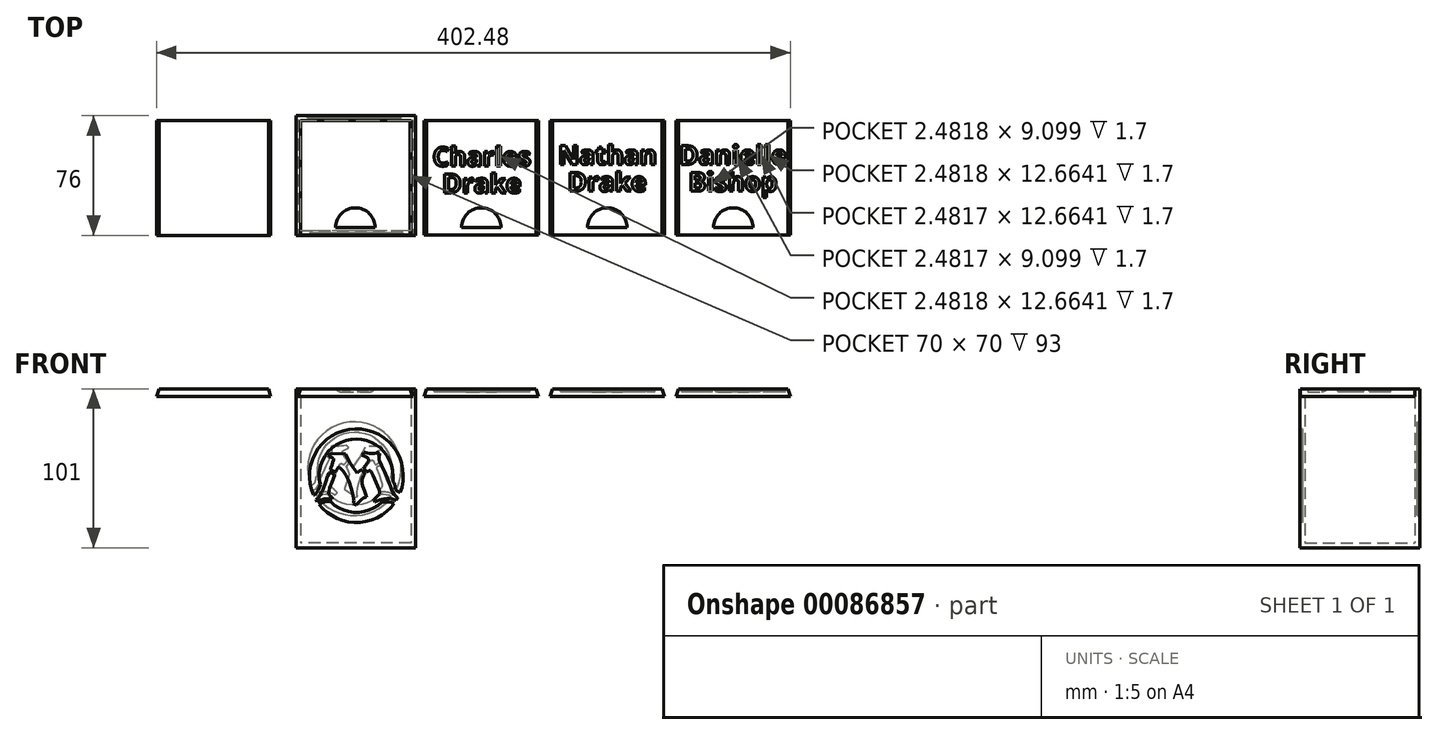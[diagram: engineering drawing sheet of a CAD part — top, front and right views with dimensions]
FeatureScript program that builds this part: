
annotation { "Feature Type Name" : "Feature", "Feature Type Description" : "" }
export const myFeature = defineFeature(function(context is Context, id is Id, definition is map)
    precondition{}
    {
        {
            var Q0;
            Q0=qCreatedBy(makeId("Top.planeOp"),FACE);
            var sketch = newSketch(context, id + "F0", { "sketchPlane" : qUnion([Q0])});
            skLineSegment(sketch, "E0.bottom", {"start": v(35, -35) * mm, "end": v(-35, -35) * mm});
            skLineSegment(sketch, "E0.top", {"start": v(35, 35) * mm, "end": v(-35, 35) * mm});
            skLineSegment(sketch, "E0.left", {"start": v(35, -35) * mm, "end": v(35, 35) * mm});
            skLineSegment(sketch, "E0.right", {"start": v(-35, -35) * mm, "end": v(-35, 35) * mm});
            skPoint(sketch, "E0.middle", {"position": v(0, 0) * mm});
            skLineSegment(sketch, "E1.0", {"start": v(38, 38) * mm, "end": v(-38, 38) * mm});
            skLineSegment(sketch, "E1.1", {"start": v(38, -38) * mm, "end": v(38, 38) * mm});
            skLineSegment(sketch, "E1.2", {"start": v(38, -38) * mm, "end": v(-38, -38) * mm});
            skLineSegment(sketch, "E1.3", {"start": v(-38, -38) * mm, "end": v(-38, 38) * mm});
            skSolve(sketch);
        }
        {
            var Q0;
            Q0=makeQuery(id+"F0.imprint","IMPRINT",FACE,{"disambiguationData":[TD([[makeQuery(id+"F0.imprint","IMPRINT",EDGE,{"derivedFrom":sQuery(id+"F0.wireOp",EDGE,"E0.bottom")}),-1.0]])]});
            var Q1;
            Q1=makeQuery(id+"F0.imprint","IMPRINT",FACE,{"disambiguationData":[TD([[makeQuery(id+"F0.imprint","IMPRINT",EDGE,{"derivedFrom":sQuery(id+"F0.wireOp",EDGE,"E0.bottom")}),1.0]])]});
            extrude(context, id + "F1", {"entities" : qUnion([Q0, Q1]), "depth" : 101 * mm});
        }
        {
            var Q0;
            Q0=makeQuery(id+"F1.opExtrude","CAP_FACE",FACE,{"disambiguationData":[OSD([sQuery(id+"F0.wireOp",EDGE,"E1.0"),sQuery(id+"F0.wireOp",EDGE,"E1.1"),sQuery(id+"F0.wireOp",EDGE,"E1.2"),sQuery(id+"F0.wireOp",EDGE,"E1.3")])],"isStart":false});
            shell(context, id + "F2", {"entities" : qUnion([Q0]), "thickness" : 3 * mm});
        }
        {
            var Q0;
            Q0=makeQuery(id+"F1.opExtrude","SWEPT_FACE",FACE,{"disambiguationData":[OSD([sQuery(id+"F0.wireOp",EDGE,"E1.2")])]});
            var sketch = newSketch(context, id + "F3", { "sketchPlane" : qUnion([Q0])});
            skLineSegment(sketch, "E2", {"start": v(-4.3, 75.14) * mm, "end": v(-0.4, 75.51) * mm});
            skLineSegment(sketch, "E3", {"start": v(-8.13, 74.27) * mm, "end": v(-4.3, 75.14) * mm});
            skLineSegment(sketch, "E4", {"start": v(-11.8, 72.9) * mm, "end": v(-8.13, 74.27) * mm});
            skLineSegment(sketch, "E5", {"start": v(-15.26, 71.06) * mm, "end": v(-11.8, 72.9) * mm});
            skLineSegment(sketch, "E6", {"start": v(-18.45, 68.78) * mm, "end": v(-15.26, 71.06) * mm});
            skLineSegment(sketch, "E7", {"start": v(-21.3, 66.1) * mm, "end": v(-18.45, 68.78) * mm});
            skLineSegment(sketch, "E8", {"start": v(-23.8, 63.06) * mm, "end": v(-21.3, 66.1) * mm});
            skLineSegment(sketch, "E9", {"start": v(-25.85, 59.73) * mm, "end": v(-23.8, 63.06) * mm});
            skLineSegment(sketch, "E10", {"start": v(-27.46, 56.16) * mm, "end": v(-25.85, 59.73) * mm});
            skLineSegment(sketch, "E11", {"start": v(-28.58, 52.4) * mm, "end": v(-27.46, 56.16) * mm});
            skLineSegment(sketch, "E12", {"start": v(-29.2, 48.53) * mm, "end": v(-28.58, 52.4) * mm});
            skLineSegment(sketch, "E13", {"start": v(-29.31, 44.61) * mm, "end": v(-29.2, 48.53) * mm});
            skLineSegment(sketch, "E14", {"start": v(-28.9, 40.72) * mm, "end": v(-29.31, 44.61) * mm});
            skLineSegment(sketch, "E15", {"start": v(-27.98, 36.9) * mm, "end": v(-28.9, 40.72) * mm});
            skLineSegment(sketch, "E16", {"start": v(-26.65, 33.46) * mm, "end": v(-27.98, 36.9) * mm});
            skLineSegment(sketch, "E17", {"start": v(-26.36, 33.55) * mm, "end": v(-26.65, 33.46) * mm});
            skLineSegment(sketch, "E18", {"start": v(-26.15, 33.66) * mm, "end": v(-26.36, 33.55) * mm});
            skLineSegment(sketch, "E19", {"start": v(-25.97, 33.78) * mm, "end": v(-26.15, 33.66) * mm});
            skLineSegment(sketch, "E20", {"start": v(-25.26, 34.57) * mm, "end": v(-25.97, 33.78) * mm});
            skLineSegment(sketch, "E21", {"start": v(-24.07, 36.37) * mm, "end": v(-25.26, 34.57) * mm});
            skLineSegment(sketch, "E22", {"start": v(-22.46, 40.36) * mm, "end": v(-24.07, 36.37) * mm});
            skLineSegment(sketch, "E23", {"start": v(-23, 42.05) * mm, "end": v(-22.46, 40.36) * mm});
            skLineSegment(sketch, "E24", {"start": v(-23.3, 43.9) * mm, "end": v(-23, 42.05) * mm});
            skLineSegment(sketch, "E25", {"start": v(-23.33, 45.77) * mm, "end": v(-23.3, 43.9) * mm});
            skLineSegment(sketch, "E26", {"start": v(-23.33, 46.03) * mm, "end": v(-23.33, 45.77) * mm});
            skLineSegment(sketch, "E27", {"start": v(-23.33, 46.29) * mm, "end": v(-23.33, 46.03) * mm});
            skLineSegment(sketch, "E28", {"start": v(-23.3, 46.8) * mm, "end": v(-23.33, 46.29) * mm});
            skLineSegment(sketch, "E29", {"start": v(-23.24, 47.82) * mm, "end": v(-23.3, 46.8) * mm});
            skLineSegment(sketch, "E30", {"start": v(-23.08, 49.13) * mm, "end": v(-23.24, 47.82) * mm});
            skLineSegment(sketch, "E31", {"start": v(-22.36, 52.4) * mm, "end": v(-23.08, 49.13) * mm});
            skLineSegment(sketch, "E32", {"start": v(-21.16, 55.55) * mm, "end": v(-22.36, 52.4) * mm});
            skLineSegment(sketch, "E33", {"start": v(-19.53, 58.49) * mm, "end": v(-21.16, 55.55) * mm});
            skLineSegment(sketch, "E34", {"start": v(-17.49, 61.16) * mm, "end": v(-19.53, 58.49) * mm});
            skLineSegment(sketch, "E35", {"start": v(-15.09, 63.51) * mm, "end": v(-17.49, 61.16) * mm});
            skLineSegment(sketch, "E36", {"start": v(-12.37, 65.5) * mm, "end": v(-15.09, 63.51) * mm});
            skLineSegment(sketch, "E37", {"start": v(-9.4, 67.06) * mm, "end": v(-12.37, 65.5) * mm});
            skLineSegment(sketch, "E38", {"start": v(-6.23, 68.19) * mm, "end": v(-9.4, 67.06) * mm});
            skLineSegment(sketch, "E39", {"start": v(-2.94, 68.84) * mm, "end": v(-6.23, 68.19) * mm});
            skLineSegment(sketch, "E40", {"start": v(-2.85, 68.86) * mm, "end": v(-2.94, 68.84) * mm});
            skLineSegment(sketch, "E41", {"start": v(-2.77, 68.87) * mm, "end": v(-2.85, 68.86) * mm});
            skLineSegment(sketch, "E42", {"start": v(-2.6, 68.88) * mm, "end": v(-2.77, 68.87) * mm});
            skLineSegment(sketch, "E43", {"start": v(-2.26, 68.92) * mm, "end": v(-2.6, 68.88) * mm});
            skLineSegment(sketch, "E44", {"start": v(0.42, 69.02) * mm, "end": v(-2.26, 68.92) * mm});
            skLineSegment(sketch, "E45", {"start": v(3.73, 68.79) * mm, "end": v(0.42, 69.02) * mm});
            skLineSegment(sketch, "E46", {"start": v(6.97, 68.08) * mm, "end": v(3.73, 68.79) * mm});
            skLineSegment(sketch, "E47", {"start": v(10.08, 66.92) * mm, "end": v(6.97, 68.08) * mm});
            skLineSegment(sketch, "E48", {"start": v(12.99, 65.33) * mm, "end": v(10.08, 66.92) * mm});
            skLineSegment(sketch, "E49", {"start": v(15.64, 63.34) * mm, "end": v(12.99, 65.33) * mm});
            skLineSegment(sketch, "E50", {"start": v(17.99, 61) * mm, "end": v(15.64, 63.34) * mm});
            skLineSegment(sketch, "E51", {"start": v(19.98, 58.34) * mm, "end": v(17.99, 61) * mm});
            skLineSegment(sketch, "E52", {"start": v(21.57, 55.43) * mm, "end": v(19.98, 58.34) * mm});
            skLineSegment(sketch, "E53", {"start": v(22.73, 52.32) * mm, "end": v(21.57, 55.43) * mm});
            skLineSegment(sketch, "E54", {"start": v(23.43, 49.09) * mm, "end": v(22.73, 52.32) * mm});
            skLineSegment(sketch, "E55", {"start": v(23.44, 49) * mm, "end": v(23.43, 49.09) * mm});
            skLineSegment(sketch, "E56", {"start": v(23.45, 48.92) * mm, "end": v(23.44, 49) * mm});
            skLineSegment(sketch, "E57", {"start": v(23.47, 48.75) * mm, "end": v(23.45, 48.92) * mm});
            skLineSegment(sketch, "E58", {"start": v(23.52, 48.42) * mm, "end": v(23.47, 48.75) * mm});
            skLineSegment(sketch, "E59", {"start": v(23.67, 45.78) * mm, "end": v(23.52, 48.42) * mm});
            skLineSegment(sketch, "E60", {"start": v(23.65, 42.52) * mm, "end": v(23.67, 45.78) * mm});
            skLineSegment(sketch, "E61", {"start": v(23.69, 42.15) * mm, "end": v(23.65, 42.52) * mm});
            skLineSegment(sketch, "E62", {"start": v(23.79, 41.8) * mm, "end": v(23.69, 42.15) * mm});
            skLineSegment(sketch, "E63", {"start": v(24.17, 41.13) * mm, "end": v(23.79, 41.8) * mm});
            skLineSegment(sketch, "E64", {"start": v(24.62, 40.42) * mm, "end": v(24.17, 41.13) * mm});
            skLineSegment(sketch, "E65", {"start": v(24.77, 40) * mm, "end": v(24.62, 40.42) * mm});
            skLineSegment(sketch, "E66", {"start": v(24.85, 39.58) * mm, "end": v(24.77, 40) * mm});
            skLineSegment(sketch, "E67", {"start": v(25.07, 37.97) * mm, "end": v(24.85, 39.58) * mm});
            skLineSegment(sketch, "E68", {"start": v(25.33, 37.24) * mm, "end": v(25.07, 37.97) * mm});
            skLineSegment(sketch, "E69", {"start": v(25.51, 36.92) * mm, "end": v(25.33, 37.24) * mm});
            skLineSegment(sketch, "E70", {"start": v(25.74, 36.63) * mm, "end": v(25.51, 36.92) * mm});
            skLineSegment(sketch, "E71", {"start": v(26.32, 36.12) * mm, "end": v(25.74, 36.63) * mm});
            skLineSegment(sketch, "E72", {"start": v(27, 35.67) * mm, "end": v(26.32, 36.12) * mm});
            skLineSegment(sketch, "E73", {"start": v(28.14, 35.03) * mm, "end": v(27, 35.67) * mm});
            skLineSegment(sketch, "E74", {"start": v(29.26, 38.49) * mm, "end": v(28.14, 35.03) * mm});
            skLineSegment(sketch, "E75", {"start": v(29.97, 42.34) * mm, "end": v(29.26, 38.49) * mm});
            skLineSegment(sketch, "E76", {"start": v(30.16, 46.26) * mm, "end": v(29.97, 42.34) * mm});
            skLineSegment(sketch, "E77", {"start": v(29.84, 50.16) * mm, "end": v(30.16, 46.26) * mm});
            skLineSegment(sketch, "E78", {"start": v(29, 54) * mm, "end": v(29.84, 50.16) * mm});
            skLineSegment(sketch, "E79", {"start": v(27.68, 57.68) * mm, "end": v(29, 54) * mm});
            skLineSegment(sketch, "E80", {"start": v(25.88, 61.16) * mm, "end": v(27.68, 57.68) * mm});
            skLineSegment(sketch, "E81", {"start": v(23.63, 64.37) * mm, "end": v(25.88, 61.16) * mm});
            skLineSegment(sketch, "E82", {"start": v(20.99, 67.26) * mm, "end": v(23.63, 64.37) * mm});
            skLineSegment(sketch, "E83", {"start": v(17.98, 69.78) * mm, "end": v(20.99, 67.26) * mm});
            skLineSegment(sketch, "E84", {"start": v(14.67, 71.88) * mm, "end": v(17.98, 69.78) * mm});
            skLineSegment(sketch, "E85", {"start": v(11.12, 73.53) * mm, "end": v(14.67, 71.88) * mm});
            skLineSegment(sketch, "E86", {"start": v(7.38, 74.7) * mm, "end": v(11.12, 73.53) * mm});
            skLineSegment(sketch, "E87", {"start": v(3.51, 75.36) * mm, "end": v(7.38, 74.7) * mm});
            skLineSegment(sketch, "E88", {"start": v(-0.4, 75.51) * mm, "end": v(3.51, 75.36) * mm});
            skLineSegment(sketch, "E89", {"start": v(6.66, 32.96) * mm, "end": v(6.68, 32.9) * mm});
            skLineSegment(sketch, "E90", {"start": v(6.65, 33.01) * mm, "end": v(6.66, 32.96) * mm});
            skLineSegment(sketch, "E91", {"start": v(6.61, 33.12) * mm, "end": v(6.65, 33.01) * mm});
            skLineSegment(sketch, "E92", {"start": v(6.55, 33.33) * mm, "end": v(6.61, 33.12) * mm});
            skLineSegment(sketch, "E93", {"start": v(5.67, 36.09) * mm, "end": v(6.55, 33.33) * mm});
            skLineSegment(sketch, "E94", {"start": v(4.49, 39.23) * mm, "end": v(5.67, 36.09) * mm});
            skLineSegment(sketch, "E95", {"start": v(4.05, 40.87) * mm, "end": v(4.49, 39.23) * mm});
            skLineSegment(sketch, "E96", {"start": v(3.93, 41.74) * mm, "end": v(4.05, 40.87) * mm});
            skLineSegment(sketch, "E97", {"start": v(3.93, 42.61) * mm, "end": v(3.93, 41.74) * mm});
            skLineSegment(sketch, "E98", {"start": v(4.06, 43.48) * mm, "end": v(3.93, 42.61) * mm});
            skLineSegment(sketch, "E99", {"start": v(4.3, 44.31) * mm, "end": v(4.06, 43.48) * mm});
            skLineSegment(sketch, "E100", {"start": v(4.98, 45.9) * mm, "end": v(4.3, 44.31) * mm});
            skLineSegment(sketch, "E101", {"start": v(5.57, 46.73) * mm, "end": v(4.98, 45.9) * mm});
            skLineSegment(sketch, "E102", {"start": v(5.59, 46.79) * mm, "end": v(5.57, 46.73) * mm});
            skLineSegment(sketch, "E103", {"start": v(5.6, 46.86) * mm, "end": v(5.59, 46.79) * mm});
            skLineSegment(sketch, "E104", {"start": v(5.57, 47.1) * mm, "end": v(5.6, 46.86) * mm});
            skLineSegment(sketch, "E105", {"start": v(5.54, 47.33) * mm, "end": v(5.57, 47.1) * mm});
            skLineSegment(sketch, "E106", {"start": v(5.51, 47.42) * mm, "end": v(5.54, 47.33) * mm});
            skLineSegment(sketch, "E107", {"start": v(5.5, 47.46) * mm, "end": v(5.51, 47.42) * mm});
            skLineSegment(sketch, "E108", {"start": v(4.16, 49) * mm, "end": v(5.5, 47.46) * mm});
            skLineSegment(sketch, "E109", {"start": v(4, 49.15) * mm, "end": v(4.16, 49) * mm});
            skLineSegment(sketch, "E110", {"start": v(3.82, 49.26) * mm, "end": v(4, 49.15) * mm});
            skLineSegment(sketch, "E111", {"start": v(3.64, 49.33) * mm, "end": v(3.82, 49.26) * mm});
            skLineSegment(sketch, "E112", {"start": v(3.44, 49.35) * mm, "end": v(3.64, 49.33) * mm});
            skLineSegment(sketch, "E113", {"start": v(2.98, 49.29) * mm, "end": v(3.44, 49.35) * mm});
            skLineSegment(sketch, "E114", {"start": v(2.78, 49.23) * mm, "end": v(2.98, 49.29) * mm});
            skLineSegment(sketch, "E115", {"start": v(2.6, 49.13) * mm, "end": v(2.78, 49.23) * mm});
            skLineSegment(sketch, "E116", {"start": v(0.88, 47.6) * mm, "end": v(2.6, 49.13) * mm});
            skLineSegment(sketch, "E117", {"start": v(0.21, 48.5) * mm, "end": v(0.88, 47.6) * mm});
            skLineSegment(sketch, "E118", {"start": v(-1.7, 51.18) * mm, "end": v(0.21, 48.5) * mm});
            skLineSegment(sketch, "E119", {"start": v(-3.45, 53.97) * mm, "end": v(-1.7, 51.18) * mm});
            skLineSegment(sketch, "E120", {"start": v(-3.45, 53.97) * mm, "end": v(-5.11, 56.82) * mm});
            skLineSegment(sketch, "E121", {"start": v(-5.11, 56.82) * mm, "end": v(-6.54, 59.63) * mm});
            skLineSegment(sketch, "E122", {"start": v(-16.46, 59.92) * mm, "end": v(-6.54, 59.63) * mm});
            skLineSegment(sketch, "E123", {"start": v(-17.38, 58.63) * mm, "end": v(-16.46, 59.92) * mm});
            skLineSegment(sketch, "E124", {"start": v(-17.61, 58.29) * mm, "end": v(-17.38, 58.63) * mm});
            skLineSegment(sketch, "E125", {"start": v(-17.55, 58.21) * mm, "end": v(-17.61, 58.29) * mm});
            skLineSegment(sketch, "E126", {"start": v(-17.24, 57.94) * mm, "end": v(-17.55, 58.21) * mm});
            skLineSegment(sketch, "E127", {"start": v(-17.1, 57.86) * mm, "end": v(-17.24, 57.94) * mm});
            skLineSegment(sketch, "E128", {"start": v(-16.95, 57.8) * mm, "end": v(-17.1, 57.86) * mm});
            skLineSegment(sketch, "E129", {"start": v(-16.1, 57.7) * mm, "end": v(-16.95, 57.8) * mm});
            skLineSegment(sketch, "E130", {"start": v(-15.27, 57.4) * mm, "end": v(-16.1, 57.7) * mm});
            skLineSegment(sketch, "E131", {"start": v(-14.83, 57.2) * mm, "end": v(-15.27, 57.4) * mm});
            skLineSegment(sketch, "E132", {"start": v(-14.6, 57.08) * mm, "end": v(-14.83, 57.2) * mm});
            skLineSegment(sketch, "E133", {"start": v(-14.4, 56.92) * mm, "end": v(-14.6, 57.08) * mm});
            skLineSegment(sketch, "E134", {"start": v(-14.3, 56.8) * mm, "end": v(-14.4, 56.92) * mm});
            skLineSegment(sketch, "E135", {"start": v(-14.22, 56.66) * mm, "end": v(-14.3, 56.8) * mm});
            skLineSegment(sketch, "E136", {"start": v(-14.18, 56.52) * mm, "end": v(-14.22, 56.66) * mm});
            skLineSegment(sketch, "E137", {"start": v(-14.17, 56.37) * mm, "end": v(-14.18, 56.52) * mm});
            skLineSegment(sketch, "E138", {"start": v(-14.2, 55.88) * mm, "end": v(-14.17, 56.37) * mm});
            skLineSegment(sketch, "E139", {"start": v(-14.58, 54.18) * mm, "end": v(-14.2, 55.88) * mm});
            skLineSegment(sketch, "E140", {"start": v(-15.2, 52.54) * mm, "end": v(-14.58, 54.18) * mm});
            skLineSegment(sketch, "E141", {"start": v(-15.82, 50.95) * mm, "end": v(-15.2, 52.54) * mm});
            skLineSegment(sketch, "E142", {"start": v(-15.96, 50.54) * mm, "end": v(-15.82, 50.95) * mm});
            skLineSegment(sketch, "E143", {"start": v(-16.04, 50.16) * mm, "end": v(-15.96, 50.54) * mm});
            skLineSegment(sketch, "E144", {"start": v(-16.03, 50.02) * mm, "end": v(-16.04, 50.16) * mm});
            skLineSegment(sketch, "E145", {"start": v(-15.99, 49.87) * mm, "end": v(-16.03, 50.02) * mm});
            skLineSegment(sketch, "E146", {"start": v(-15.9, 49.73) * mm, "end": v(-15.99, 49.87) * mm});
            skLineSegment(sketch, "E147", {"start": v(-15.8, 49.6) * mm, "end": v(-15.9, 49.73) * mm});
            skLineSegment(sketch, "E148", {"start": v(-15.65, 49.5) * mm, "end": v(-15.8, 49.6) * mm});
            skLineSegment(sketch, "E149", {"start": v(-15.49, 49.42) * mm, "end": v(-15.65, 49.5) * mm});
            skLineSegment(sketch, "E150", {"start": v(-15.09, 49.27) * mm, "end": v(-15.49, 49.42) * mm});
            skLineSegment(sketch, "E151", {"start": v(-14.3, 48.91) * mm, "end": v(-15.09, 49.27) * mm});
            skLineSegment(sketch, "E152", {"start": v(-13.51, 48.5) * mm, "end": v(-14.3, 48.91) * mm});
            skLineSegment(sketch, "E153", {"start": v(-13.34, 48.44) * mm, "end": v(-13.51, 48.5) * mm});
            skLineSegment(sketch, "E154", {"start": v(-13.18, 48.4) * mm, "end": v(-13.34, 48.44) * mm});
            skLineSegment(sketch, "E155", {"start": v(-13.11, 48.4) * mm, "end": v(-13.18, 48.4) * mm});
            skLineSegment(sketch, "E156", {"start": v(-13.05, 48.41) * mm, "end": v(-13.11, 48.4) * mm});
            skLineSegment(sketch, "E157", {"start": v(-12.9, 48.46) * mm, "end": v(-13.05, 48.41) * mm});
            skLineSegment(sketch, "E158", {"start": v(-12.75, 48.55) * mm, "end": v(-12.9, 48.46) * mm});
            skLineSegment(sketch, "E159", {"start": v(-12.62, 48.66) * mm, "end": v(-12.75, 48.55) * mm});
            skLineSegment(sketch, "E160", {"start": v(-12.38, 48.98) * mm, "end": v(-12.62, 48.66) * mm});
            skLineSegment(sketch, "E161", {"start": v(-12, 49.71) * mm, "end": v(-12.38, 48.98) * mm});
            skLineSegment(sketch, "E162", {"start": v(-11.65, 50.54) * mm, "end": v(-12, 49.71) * mm});
            skLineSegment(sketch, "E163", {"start": v(-11.54, 50.76) * mm, "end": v(-11.65, 50.54) * mm});
            skLineSegment(sketch, "E164", {"start": v(-11.47, 50.88) * mm, "end": v(-11.54, 50.76) * mm});
            skLineSegment(sketch, "E165", {"start": v(-11.36, 51) * mm, "end": v(-11.47, 50.88) * mm});
            skLineSegment(sketch, "E166", {"start": v(-11.24, 51.08) * mm, "end": v(-11.36, 51) * mm});
            skLineSegment(sketch, "E167", {"start": v(-11.08, 51.13) * mm, "end": v(-11.24, 51.08) * mm});
            skLineSegment(sketch, "E168", {"start": v(-10.93, 51.15) * mm, "end": v(-11.08, 51.13) * mm});
            skLineSegment(sketch, "E169", {"start": v(-10.78, 51.14) * mm, "end": v(-10.93, 51.15) * mm});
            skLineSegment(sketch, "E170", {"start": v(-10.52, 51.09) * mm, "end": v(-10.78, 51.14) * mm});
            skLineSegment(sketch, "E171", {"start": v(-10.28, 51) * mm, "end": v(-10.52, 51.09) * mm});
            skLineSegment(sketch, "E172", {"start": v(-9.88, 50.75) * mm, "end": v(-10.28, 51) * mm});
            skLineSegment(sketch, "E173", {"start": v(-9.88, 50.75) * mm, "end": v(-9.18, 50.19) * mm});
            skLineSegment(sketch, "E174", {"start": v(-9.18, 50.19) * mm, "end": v(-8, 48.88) * mm});
            skLineSegment(sketch, "E175", {"start": v(-6.22, 45.9) * mm, "end": v(-8, 48.88) * mm});
            skLineSegment(sketch, "E176", {"start": v(-4.98, 43.52) * mm, "end": v(-6.22, 45.9) * mm});
            skLineSegment(sketch, "E177", {"start": v(-3.87, 41.07) * mm, "end": v(-4.98, 43.52) * mm});
            skLineSegment(sketch, "E178", {"start": v(-2.37, 35.93) * mm, "end": v(-3.87, 41.07) * mm});
            skLineSegment(sketch, "E179", {"start": v(-1.74, 33.34) * mm, "end": v(-2.37, 35.93) * mm});
            skLineSegment(sketch, "E180", {"start": v(-1.23, 30.68) * mm, "end": v(-1.74, 33.34) * mm});
            skLineSegment(sketch, "E181", {"start": v(-1.17, 29.98) * mm, "end": v(-1.23, 30.68) * mm});
            skLineSegment(sketch, "E182", {"start": v(-1.25, 29.28) * mm, "end": v(-1.17, 29.98) * mm});
            skLineSegment(sketch, "E183", {"start": v(-1.41, 28.6) * mm, "end": v(-1.25, 29.28) * mm});
            skLineSegment(sketch, "E184", {"start": v(-1.48, 28.42) * mm, "end": v(-1.41, 28.6) * mm});
            skLineSegment(sketch, "E185", {"start": v(-1.56, 28.25) * mm, "end": v(-1.48, 28.42) * mm});
            skLineSegment(sketch, "E186", {"start": v(-1.6, 28.2) * mm, "end": v(-1.56, 28.25) * mm});
            skLineSegment(sketch, "E187", {"start": v(-1.47, 28.17) * mm, "end": v(-1.6, 28.2) * mm});
            skLineSegment(sketch, "E188", {"start": v(-1.11, 28.02) * mm, "end": v(-1.47, 28.17) * mm});
            skLineSegment(sketch, "E189", {"start": v(-0.54, 27.67) * mm, "end": v(-1.11, 28.02) * mm});
            skLineSegment(sketch, "E190", {"start": v(0.02, 27.33) * mm, "end": v(-0.54, 27.67) * mm});
            skLineSegment(sketch, "E191", {"start": v(0.32, 27.12) * mm, "end": v(0.02, 27.33) * mm});
            skLineSegment(sketch, "E192", {"start": v(0.44, 27) * mm, "end": v(0.32, 27.12) * mm});
            skLineSegment(sketch, "E193", {"start": v(0.59, 27.4) * mm, "end": v(0.44, 27) * mm});
            skLineSegment(sketch, "E194", {"start": v(0.9, 27.88) * mm, "end": v(0.59, 27.4) * mm});
            skLineSegment(sketch, "E195", {"start": v(1.67, 28.68) * mm, "end": v(0.9, 27.88) * mm});
            skLineSegment(sketch, "E196", {"start": v(3.2, 30.22) * mm, "end": v(1.67, 28.68) * mm});
            skLineSegment(sketch, "E197", {"start": v(4, 31) * mm, "end": v(3.2, 30.22) * mm});
            skLineSegment(sketch, "E198", {"start": v(4.91, 31.58) * mm, "end": v(4, 31) * mm});
            skLineSegment(sketch, "E199", {"start": v(5.87, 32.16) * mm, "end": v(4.91, 31.58) * mm});
            skLineSegment(sketch, "E200", {"start": v(6.14, 32.3) * mm, "end": v(5.87, 32.16) * mm});
            skLineSegment(sketch, "E201", {"start": v(6.43, 32.39) * mm, "end": v(6.14, 32.3) * mm});
            skLineSegment(sketch, "E202", {"start": v(6.73, 32.43) * mm, "end": v(6.43, 32.39) * mm});
            skLineSegment(sketch, "E203", {"start": v(6.77, 32.43) * mm, "end": v(6.73, 32.43) * mm});
            skLineSegment(sketch, "E204", {"start": v(6.77, 32.55) * mm, "end": v(6.77, 32.43) * mm});
            skLineSegment(sketch, "E205", {"start": v(6.68, 32.9) * mm, "end": v(6.77, 32.55) * mm});
            skLineSegment(sketch, "E206", {"start": v(18.8, 47.07) * mm, "end": v(19.43, 45.67) * mm});
            skLineSegment(sketch, "E207", {"start": v(16.23, 52.35) * mm, "end": v(18.8, 47.07) * mm});
            skLineSegment(sketch, "E208", {"start": v(15.16, 55.1) * mm, "end": v(16.23, 52.35) * mm});
            skLineSegment(sketch, "E209", {"start": v(14.95, 55.83) * mm, "end": v(15.16, 55.1) * mm});
            skLineSegment(sketch, "E210", {"start": v(14.87, 56.6) * mm, "end": v(14.95, 55.83) * mm});
            skLineSegment(sketch, "E211", {"start": v(14.94, 58.1) * mm, "end": v(14.87, 56.6) * mm});
            skLineSegment(sketch, "E212", {"start": v(15.07, 59.54) * mm, "end": v(14.94, 58.1) * mm});
            skLineSegment(sketch, "E213", {"start": v(15.07, 59.71) * mm, "end": v(15.07, 59.54) * mm});
            skLineSegment(sketch, "E214", {"start": v(15.05, 59.86) * mm, "end": v(15.07, 59.71) * mm});
            skLineSegment(sketch, "E215", {"start": v(15.03, 59.9) * mm, "end": v(15.05, 59.86) * mm});
            skLineSegment(sketch, "E216", {"start": v(15, 59.94) * mm, "end": v(15.03, 59.9) * mm});
            skLineSegment(sketch, "E217", {"start": v(14.95, 59.97) * mm, "end": v(15, 59.94) * mm});
            skLineSegment(sketch, "E218", {"start": v(14.3, 60.33) * mm, "end": v(14.95, 59.97) * mm});
            skLineSegment(sketch, "E219", {"start": v(14, 60.5) * mm, "end": v(14.3, 60.33) * mm});
            skLineSegment(sketch, "E220", {"start": v(13.95, 60.53) * mm, "end": v(14, 60.5) * mm});
            skLineSegment(sketch, "E221", {"start": v(13.91, 60.54) * mm, "end": v(13.95, 60.53) * mm});
            skLineSegment(sketch, "E222", {"start": v(13.87, 60.54) * mm, "end": v(13.91, 60.54) * mm});
            skLineSegment(sketch, "E223", {"start": v(13.82, 60.54) * mm, "end": v(13.87, 60.54) * mm});
            skLineSegment(sketch, "E224", {"start": v(13.12, 60.3) * mm, "end": v(13.82, 60.54) * mm});
            skLineSegment(sketch, "E225", {"start": v(11.66, 60.01) * mm, "end": v(13.12, 60.3) * mm});
            skLineSegment(sketch, "E226", {"start": v(10.16, 59.92) * mm, "end": v(11.66, 60.01) * mm});
            skLineSegment(sketch, "E227", {"start": v(8.68, 60.06) * mm, "end": v(10.16, 59.92) * mm});
            skLineSegment(sketch, "E228", {"start": v(7.2, 60.19) * mm, "end": v(8.68, 60.06) * mm});
            skLineSegment(sketch, "E229", {"start": v(5.78, 60.6) * mm, "end": v(7.2, 60.19) * mm});
            skLineSegment(sketch, "E230", {"start": v(5.63, 60.63) * mm, "end": v(5.78, 60.6) * mm});
            skLineSegment(sketch, "E231", {"start": v(5.5, 60.63) * mm, "end": v(5.63, 60.63) * mm});
            skLineSegment(sketch, "E232", {"start": v(5.47, 60.63) * mm, "end": v(5.5, 60.63) * mm});
            skLineSegment(sketch, "E233", {"start": v(5.43, 60.6) * mm, "end": v(5.47, 60.63) * mm});
            skLineSegment(sketch, "E234", {"start": v(5.33, 60.53) * mm, "end": v(5.43, 60.6) * mm});
            skLineSegment(sketch, "E235", {"start": v(4.85, 60) * mm, "end": v(5.33, 60.53) * mm});
            skLineSegment(sketch, "E236", {"start": v(4.4, 59.46) * mm, "end": v(4.85, 60) * mm});
            skLineSegment(sketch, "E237", {"start": v(4.22, 59.18) * mm, "end": v(4.4, 59.46) * mm});
            skLineSegment(sketch, "E238", {"start": v(4.17, 59.05) * mm, "end": v(4.22, 59.18) * mm});
            skLineSegment(sketch, "E239", {"start": v(4.15, 58.91) * mm, "end": v(4.17, 59.05) * mm});
            skLineSegment(sketch, "E240", {"start": v(4.15, 58.86) * mm, "end": v(4.15, 58.91) * mm});
            skLineSegment(sketch, "E241", {"start": v(4.18, 58.84) * mm, "end": v(4.15, 58.86) * mm});
            skLineSegment(sketch, "E242", {"start": v(4.3, 58.78) * mm, "end": v(4.18, 58.84) * mm});
            skLineSegment(sketch, "E243", {"start": v(4.49, 58.71) * mm, "end": v(4.3, 58.78) * mm});
            skLineSegment(sketch, "E244", {"start": v(5.24, 58.42) * mm, "end": v(4.49, 58.71) * mm});
            skLineSegment(sketch, "E245", {"start": v(6.52, 57.74) * mm, "end": v(5.24, 58.42) * mm});
            skLineSegment(sketch, "E246", {"start": v(7.15, 57.36) * mm, "end": v(6.52, 57.74) * mm});
            skLineSegment(sketch, "E247", {"start": v(7.48, 57.14) * mm, "end": v(7.15, 57.36) * mm});
            skLineSegment(sketch, "E248", {"start": v(7.78, 56.86) * mm, "end": v(7.48, 57.14) * mm});
            skLineSegment(sketch, "E249", {"start": v(8.02, 56.53) * mm, "end": v(7.78, 56.86) * mm});
            skLineSegment(sketch, "E250", {"start": v(8.2, 56.14) * mm, "end": v(8.02, 56.53) * mm});
            skLineSegment(sketch, "E251", {"start": v(8.25, 55.92) * mm, "end": v(8.2, 56.14) * mm});
            skLineSegment(sketch, "E252", {"start": v(8.27, 55.69) * mm, "end": v(8.25, 55.92) * mm});
            skLineSegment(sketch, "E253", {"start": v(8.23, 55.46) * mm, "end": v(8.27, 55.69) * mm});
            skLineSegment(sketch, "E254", {"start": v(8.15, 55.24) * mm, "end": v(8.23, 55.46) * mm});
            skLineSegment(sketch, "E255", {"start": v(7.25, 54) * mm, "end": v(8.15, 55.24) * mm});
            skLineSegment(sketch, "E256", {"start": v(6.54, 52.75) * mm, "end": v(7.25, 54) * mm});
            skLineSegment(sketch, "E257", {"start": v(6.1, 52.11) * mm, "end": v(6.54, 52.75) * mm});
            skLineSegment(sketch, "E258", {"start": v(5.53, 51.57) * mm, "end": v(6.1, 52.11) * mm});
            skLineSegment(sketch, "E259", {"start": v(5.25, 51.32) * mm, "end": v(5.53, 51.57) * mm});
            skLineSegment(sketch, "E260", {"start": v(5.16, 51.21) * mm, "end": v(5.25, 51.32) * mm});
            skLineSegment(sketch, "E261", {"start": v(5.1, 51.1) * mm, "end": v(5.16, 51.21) * mm});
            skLineSegment(sketch, "E262", {"start": v(5.06, 51) * mm, "end": v(5.1, 51.1) * mm});
            skLineSegment(sketch, "E263", {"start": v(5.05, 50.86) * mm, "end": v(5.06, 51) * mm});
            skLineSegment(sketch, "E264", {"start": v(5.06, 50.73) * mm, "end": v(5.05, 50.86) * mm});
            skLineSegment(sketch, "E265", {"start": v(5.1, 50.6) * mm, "end": v(5.06, 50.73) * mm});
            skLineSegment(sketch, "E266", {"start": v(5.26, 50.3) * mm, "end": v(5.1, 50.6) * mm});
            skLineSegment(sketch, "E267", {"start": v(5.46, 50.03) * mm, "end": v(5.26, 50.3) * mm});
            skLineSegment(sketch, "E268", {"start": v(5.91, 49.48) * mm, "end": v(5.46, 50.03) * mm});
            skLineSegment(sketch, "E269", {"start": v(6.4, 48.94) * mm, "end": v(5.91, 49.48) * mm});
            skLineSegment(sketch, "E270", {"start": v(6.65, 48.68) * mm, "end": v(6.4, 48.94) * mm});
            skLineSegment(sketch, "E271", {"start": v(6.77, 48.59) * mm, "end": v(6.65, 48.68) * mm});
            skLineSegment(sketch, "E272", {"start": v(6.89, 48.52) * mm, "end": v(6.77, 48.59) * mm});
            skLineSegment(sketch, "E273", {"start": v(7.02, 48.47) * mm, "end": v(6.89, 48.52) * mm});
            skLineSegment(sketch, "E274", {"start": v(7.17, 48.43) * mm, "end": v(7.02, 48.47) * mm});
            skLineSegment(sketch, "E275", {"start": v(7.51, 48.4) * mm, "end": v(7.17, 48.43) * mm});
            skLineSegment(sketch, "E276", {"start": v(7.56, 48.4) * mm, "end": v(7.51, 48.4) * mm});
            skLineSegment(sketch, "E277", {"start": v(7.61, 48.4) * mm, "end": v(7.56, 48.4) * mm});
            skLineSegment(sketch, "E278", {"start": v(7.65, 48.42) * mm, "end": v(7.61, 48.4) * mm});
            skLineSegment(sketch, "E279", {"start": v(7.7, 48.44) * mm, "end": v(7.65, 48.42) * mm});
            skLineSegment(sketch, "E280", {"start": v(7.97, 48.68) * mm, "end": v(7.7, 48.44) * mm});
            skLineSegment(sketch, "E281", {"start": v(8.31, 48.9) * mm, "end": v(7.97, 48.68) * mm});
            skLineSegment(sketch, "E282", {"start": v(8.53, 48.99) * mm, "end": v(8.31, 48.9) * mm});
            skLineSegment(sketch, "E283", {"start": v(8.66, 49.02) * mm, "end": v(8.53, 48.99) * mm});
            skLineSegment(sketch, "E284", {"start": v(8.8, 49.02) * mm, "end": v(8.66, 49.02) * mm});
            skLineSegment(sketch, "E285", {"start": v(8.93, 49) * mm, "end": v(8.8, 49.02) * mm});
            skLineSegment(sketch, "E286", {"start": v(9.06, 48.97) * mm, "end": v(8.93, 49) * mm});
            skLineSegment(sketch, "E287", {"start": v(9.27, 48.85) * mm, "end": v(9.06, 48.97) * mm});
            skLineSegment(sketch, "E288", {"start": v(9.45, 48.7) * mm, "end": v(9.27, 48.85) * mm});
            skLineSegment(sketch, "E289", {"start": v(9.6, 48.52) * mm, "end": v(9.45, 48.7) * mm});
            skLineSegment(sketch, "E290", {"start": v(10.95, 45.88) * mm, "end": v(9.6, 48.52) * mm});
            skLineSegment(sketch, "E291", {"start": v(14.81, 36.94) * mm, "end": v(10.95, 45.88) * mm});
            skLineSegment(sketch, "E292", {"start": v(15.17, 35.73) * mm, "end": v(14.81, 36.94) * mm});
            skLineSegment(sketch, "E293", {"start": v(15.2, 35.38) * mm, "end": v(15.17, 35.73) * mm});
            skLineSegment(sketch, "E294", {"start": v(15.17, 35.04) * mm, "end": v(15.2, 35.38) * mm});
            skLineSegment(sketch, "E295", {"start": v(15.1, 34.7) * mm, "end": v(15.17, 35.04) * mm});
            skLineSegment(sketch, "E296", {"start": v(14.97, 34.39) * mm, "end": v(15.1, 34.7) * mm});
            skLineSegment(sketch, "E297", {"start": v(14.65, 33.83) * mm, "end": v(14.97, 34.39) * mm});
            skLineSegment(sketch, "E298", {"start": v(14.24, 33.32) * mm, "end": v(14.65, 33.83) * mm});
            skLineSegment(sketch, "E299", {"start": v(13.36, 32.44) * mm, "end": v(14.24, 33.32) * mm});
            skLineSegment(sketch, "E300", {"start": v(11.6, 30.83) * mm, "end": v(13.36, 32.44) * mm});
            skLineSegment(sketch, "E301", {"start": v(11.38, 30.6) * mm, "end": v(11.6, 30.83) * mm});
            skLineSegment(sketch, "E302", {"start": v(11.28, 30.5) * mm, "end": v(11.38, 30.6) * mm});
            skLineSegment(sketch, "E303", {"start": v(11.23, 30.43) * mm, "end": v(11.28, 30.5) * mm});
            skLineSegment(sketch, "E304", {"start": v(11.45, 30.21) * mm, "end": v(11.23, 30.43) * mm});
            skLineSegment(sketch, "E305", {"start": v(11.93, 29.73) * mm, "end": v(11.45, 30.21) * mm});
            skLineSegment(sketch, "E306", {"start": v(12.26, 29.28) * mm, "end": v(11.93, 29.73) * mm});
            skLineSegment(sketch, "E307", {"start": v(12.53, 29.08) * mm, "end": v(12.26, 29.28) * mm});
            skLineSegment(sketch, "E308", {"start": v(13.65, 29.78) * mm, "end": v(12.53, 29.08) * mm});
            skLineSegment(sketch, "E309", {"start": v(15.04, 30.37) * mm, "end": v(13.65, 29.78) * mm});
            skLineSegment(sketch, "E310", {"start": v(16.47, 30.85) * mm, "end": v(15.04, 30.37) * mm});
            skLineSegment(sketch, "E311", {"start": v(17.94, 31.17) * mm, "end": v(16.47, 30.85) * mm});
            skLineSegment(sketch, "E312", {"start": v(19.98, 31.32) * mm, "end": v(17.94, 31.17) * mm});
            skLineSegment(sketch, "E313", {"start": v(22.04, 31.3) * mm, "end": v(19.98, 31.32) * mm});
            skLineSegment(sketch, "E314", {"start": v(24.05, 30.82) * mm, "end": v(22.04, 31.3) * mm});
            skLineSegment(sketch, "E315", {"start": v(25.76, 30.2) * mm, "end": v(24.05, 30.82) * mm});
            skLineSegment(sketch, "E316", {"start": v(26.06, 30.69) * mm, "end": v(25.76, 30.2) * mm});
            skLineSegment(sketch, "E317", {"start": v(26.44, 31.35) * mm, "end": v(26.06, 30.69) * mm});
            skLineSegment(sketch, "E318", {"start": v(26.68, 31.8) * mm, "end": v(26.44, 31.35) * mm});
            skLineSegment(sketch, "E319", {"start": v(26.14, 32.08) * mm, "end": v(26.68, 31.8) * mm});
            skLineSegment(sketch, "E320", {"start": v(25.45, 32.64) * mm, "end": v(26.14, 32.08) * mm});
            skLineSegment(sketch, "E321", {"start": v(24.36, 33.95) * mm, "end": v(25.45, 32.64) * mm});
            skLineSegment(sketch, "E322", {"start": v(23.38, 35.36) * mm, "end": v(24.36, 33.95) * mm});
            skLineSegment(sketch, "E323", {"start": v(23.06, 36.18) * mm, "end": v(23.38, 35.36) * mm});
            skLineSegment(sketch, "E324", {"start": v(22.87, 37) * mm, "end": v(23.06, 36.18) * mm});
            skLineSegment(sketch, "E325", {"start": v(22.21, 39.09) * mm, "end": v(22.87, 37) * mm});
            skLineSegment(sketch, "E326", {"start": v(21.29, 41.48) * mm, "end": v(22.21, 39.09) * mm});
            skLineSegment(sketch, "E327", {"start": v(19.43, 45.67) * mm, "end": v(21.29, 41.48) * mm});
            skLineSegment(sketch, "E328", {"start": v(-25.22, 30.76) * mm, "end": v(-25.1, 30.8) * mm});
            skLineSegment(sketch, "E329", {"start": v(-25.27, 30.74) * mm, "end": v(-25.22, 30.76) * mm});
            skLineSegment(sketch, "E330", {"start": v(-24.9, 29.8) * mm, "end": v(-25.27, 30.74) * mm});
            skLineSegment(sketch, "E331", {"start": v(-24.45, 29.16) * mm, "end": v(-24.9, 29.8) * mm});
            skLineSegment(sketch, "E332", {"start": v(-24.17, 29.4) * mm, "end": v(-24.45, 29.16) * mm});
            skLineSegment(sketch, "E333", {"start": v(-23.74, 29.67) * mm, "end": v(-24.17, 29.4) * mm});
            skLineSegment(sketch, "E334", {"start": v(-22.89, 30.2) * mm, "end": v(-23.74, 29.67) * mm});
            skLineSegment(sketch, "E335", {"start": v(-21.03, 30.87) * mm, "end": v(-22.89, 30.2) * mm});
            skLineSegment(sketch, "E336", {"start": v(-20.05, 31.08) * mm, "end": v(-21.03, 30.87) * mm});
            skLineSegment(sketch, "E337", {"start": v(-19.05, 31.14) * mm, "end": v(-20.05, 31.08) * mm});
            skLineSegment(sketch, "E338", {"start": v(-17.1, 31.13) * mm, "end": v(-19.05, 31.14) * mm});
            skLineSegment(sketch, "E339", {"start": v(-14.93, 30.94) * mm, "end": v(-17.1, 31.13) * mm});
            skLineSegment(sketch, "E340", {"start": v(-14.93, 31.7) * mm, "end": v(-14.93, 30.94) * mm});
            skLineSegment(sketch, "E341", {"start": v(-14.96, 31.93) * mm, "end": v(-14.93, 31.7) * mm});
            skLineSegment(sketch, "E342", {"start": v(-14.98, 32) * mm, "end": v(-14.96, 31.93) * mm});
            skLineSegment(sketch, "E343", {"start": v(-15.02, 32.08) * mm, "end": v(-14.98, 32) * mm});
            skLineSegment(sketch, "E344", {"start": v(-15.08, 32.15) * mm, "end": v(-15.02, 32.08) * mm});
            skLineSegment(sketch, "E345", {"start": v(-15.14, 32.2) * mm, "end": v(-15.08, 32.15) * mm});
            skLineSegment(sketch, "E346", {"start": v(-15.34, 32.34) * mm, "end": v(-15.14, 32.2) * mm});
            skLineSegment(sketch, "E347", {"start": v(-16.28, 32.85) * mm, "end": v(-15.34, 32.34) * mm});
            skLineSegment(sketch, "E348", {"start": v(-16.69, 33.3) * mm, "end": v(-16.28, 32.85) * mm});
            skLineSegment(sketch, "E349", {"start": v(-16.98, 33.8) * mm, "end": v(-16.69, 33.3) * mm});
            skLineSegment(sketch, "E350", {"start": v(-17.16, 34.35) * mm, "end": v(-16.98, 33.8) * mm});
            skLineSegment(sketch, "E351", {"start": v(-17.24, 34.92) * mm, "end": v(-17.16, 34.35) * mm});
            skLineSegment(sketch, "E352", {"start": v(-17.09, 36.01) * mm, "end": v(-17.24, 34.92) * mm});
            skLineSegment(sketch, "E353", {"start": v(-16.48, 38.03) * mm, "end": v(-17.09, 36.01) * mm});
            skLineSegment(sketch, "E354", {"start": v(-15.14, 42) * mm, "end": v(-16.48, 38.03) * mm});
            skLineSegment(sketch, "E355", {"start": v(-13.56, 45.83) * mm, "end": v(-15.14, 42) * mm});
            skLineSegment(sketch, "E356", {"start": v(-13.54, 46.21) * mm, "end": v(-13.56, 45.83) * mm});
            skLineSegment(sketch, "E357", {"start": v(-13.57, 46.38) * mm, "end": v(-13.54, 46.21) * mm});
            skLineSegment(sketch, "E358", {"start": v(-13.6, 46.43) * mm, "end": v(-13.57, 46.38) * mm});
            skLineSegment(sketch, "E359", {"start": v(-13.62, 46.47) * mm, "end": v(-13.6, 46.43) * mm});
            skLineSegment(sketch, "E360", {"start": v(-13.75, 46.59) * mm, "end": v(-13.62, 46.47) * mm});
            skLineSegment(sketch, "E361", {"start": v(-13.93, 46.7) * mm, "end": v(-13.75, 46.59) * mm});
            skLineSegment(sketch, "E362", {"start": v(-14.31, 46.94) * mm, "end": v(-13.93, 46.7) * mm});
            skLineSegment(sketch, "E363", {"start": v(-14.45, 47.02) * mm, "end": v(-14.31, 46.94) * mm});
            skLineSegment(sketch, "E364", {"start": v(-14.58, 47.1) * mm, "end": v(-14.45, 47.02) * mm});
            skLineSegment(sketch, "E365", {"start": v(-14.85, 47.24) * mm, "end": v(-14.58, 47.1) * mm});
            skLineSegment(sketch, "E366", {"start": v(-15.41, 47.51) * mm, "end": v(-14.85, 47.24) * mm});
            skLineSegment(sketch, "E367", {"start": v(-15.87, 47.71) * mm, "end": v(-15.41, 47.51) * mm});
            skLineSegment(sketch, "E368", {"start": v(-16.27, 47.87) * mm, "end": v(-15.87, 47.71) * mm});
            skLineSegment(sketch, "E369", {"start": v(-16.34, 47.88) * mm, "end": v(-16.27, 47.87) * mm});
            skLineSegment(sketch, "E370", {"start": v(-16.42, 47.88) * mm, "end": v(-16.34, 47.88) * mm});
            skLineSegment(sketch, "E371", {"start": v(-16.5, 47.87) * mm, "end": v(-16.42, 47.88) * mm});
            skLineSegment(sketch, "E372", {"start": v(-16.59, 47.85) * mm, "end": v(-16.5, 47.87) * mm});
            skLineSegment(sketch, "E373", {"start": v(-16.66, 47.82) * mm, "end": v(-16.59, 47.85) * mm});
            skLineSegment(sketch, "E374", {"start": v(-16.72, 47.79) * mm, "end": v(-16.66, 47.82) * mm});
            skLineSegment(sketch, "E375", {"start": v(-16.85, 47.68) * mm, "end": v(-16.72, 47.79) * mm});
            skLineSegment(sketch, "E376", {"start": v(-17.08, 47.33) * mm, "end": v(-16.85, 47.68) * mm});
            skLineSegment(sketch, "E377", {"start": v(-17.8, 45.68) * mm, "end": v(-17.08, 47.33) * mm});
            skLineSegment(sketch, "E378", {"start": v(-19.16, 41.44) * mm, "end": v(-17.8, 45.68) * mm});
            skLineSegment(sketch, "E379", {"start": v(-20.75, 37.24) * mm, "end": v(-19.16, 41.44) * mm});
            skLineSegment(sketch, "E380", {"start": v(-21.57, 35.33) * mm, "end": v(-20.75, 37.24) * mm});
            skLineSegment(sketch, "E381", {"start": v(-22.54, 33.5) * mm, "end": v(-21.57, 35.33) * mm});
            skLineSegment(sketch, "E382", {"start": v(-23.74, 31.76) * mm, "end": v(-22.54, 33.5) * mm});
            skLineSegment(sketch, "E383", {"start": v(-24.57, 31.08) * mm, "end": v(-23.74, 31.76) * mm});
            skLineSegment(sketch, "E384", {"start": v(-24.81, 30.92) * mm, "end": v(-24.57, 31.08) * mm});
            skLineSegment(sketch, "E385", {"start": v(-25.1, 30.8) * mm, "end": v(-24.81, 30.92) * mm});
            skLineSegment(sketch, "E386", {"start": v(23.82, 28.54) * mm, "end": v(24.48, 28.3) * mm});
            skLineSegment(sketch, "E387", {"start": v(22.8, 28.75) * mm, "end": v(23.82, 28.54) * mm});
            skLineSegment(sketch, "E388", {"start": v(20.7, 29.03) * mm, "end": v(22.8, 28.75) * mm});
            skLineSegment(sketch, "E389", {"start": v(18.58, 29.3) * mm, "end": v(20.7, 29.03) * mm});
            skLineSegment(sketch, "E390", {"start": v(17.55, 29.3) * mm, "end": v(18.58, 29.3) * mm});
            skLineSegment(sketch, "E391", {"start": v(16.6, 29.09) * mm, "end": v(17.55, 29.3) * mm});
            skLineSegment(sketch, "E392", {"start": v(14.16, 27.02) * mm, "end": v(16.6, 29.09) * mm});
            skLineSegment(sketch, "E393", {"start": v(11.4, 25.28) * mm, "end": v(14.16, 27.02) * mm});
            skLineSegment(sketch, "E394", {"start": v(8.4, 23.94) * mm, "end": v(11.4, 25.28) * mm});
            skLineSegment(sketch, "E395", {"start": v(5.26, 23.03) * mm, "end": v(8.4, 23.94) * mm});
            skLineSegment(sketch, "E396", {"start": v(2.01, 22.58) * mm, "end": v(5.26, 23.03) * mm});
            skLineSegment(sketch, "E397", {"start": v(-1.26, 22.58) * mm, "end": v(2.01, 22.58) * mm});
            skLineSegment(sketch, "E398", {"start": v(-4.5, 23.05) * mm, "end": v(-1.26, 22.58) * mm});
            skLineSegment(sketch, "E399", {"start": v(-7.65, 23.96) * mm, "end": v(-4.5, 23.05) * mm});
            skLineSegment(sketch, "E400", {"start": v(-10.63, 25.31) * mm, "end": v(-7.65, 23.96) * mm});
            skLineSegment(sketch, "E401", {"start": v(-13.4, 27.07) * mm, "end": v(-10.63, 25.31) * mm});
            skLineSegment(sketch, "E402", {"start": v(-15.83, 29.15) * mm, "end": v(-13.4, 27.07) * mm});
            skLineSegment(sketch, "E403", {"start": v(-16.75, 29.38) * mm, "end": v(-15.83, 29.15) * mm});
            skLineSegment(sketch, "E404", {"start": v(-17.73, 29.43) * mm, "end": v(-16.75, 29.38) * mm});
            skLineSegment(sketch, "E405", {"start": v(-19.76, 29.12) * mm, "end": v(-17.73, 29.43) * mm});
            skLineSegment(sketch, "E406", {"start": v(-21.72, 28.59) * mm, "end": v(-19.76, 29.12) * mm});
            skLineSegment(sketch, "E407", {"start": v(-22.6, 28.14) * mm, "end": v(-21.72, 28.59) * mm});
            skLineSegment(sketch, "E408", {"start": v(-23.21, 27.72) * mm, "end": v(-22.6, 28.14) * mm});
            skLineSegment(sketch, "E409", {"start": v(-20.96, 25.09) * mm, "end": v(-23.21, 27.72) * mm});
            skLineSegment(sketch, "E410", {"start": v(-18.2, 22.57) * mm, "end": v(-20.96, 25.09) * mm});
            skLineSegment(sketch, "E411", {"start": v(-15.16, 20.43) * mm, "end": v(-18.2, 22.57) * mm});
            skLineSegment(sketch, "E412", {"start": v(-11.86, 18.68) * mm, "end": v(-15.16, 20.43) * mm});
            skLineSegment(sketch, "E413", {"start": v(-8.38, 17.35) * mm, "end": v(-11.86, 18.68) * mm});
            skLineSegment(sketch, "E414", {"start": v(-4.75, 16.48) * mm, "end": v(-8.38, 17.35) * mm});
            skLineSegment(sketch, "E415", {"start": v(-1.05, 16.06) * mm, "end": v(-4.75, 16.48) * mm});
            skLineSegment(sketch, "E416", {"start": v(2.68, 16.1) * mm, "end": v(-1.05, 16.06) * mm});
            skLineSegment(sketch, "E417", {"start": v(6.38, 16.63) * mm, "end": v(2.68, 16.1) * mm});
            skLineSegment(sketch, "E418", {"start": v(9.98, 17.6) * mm, "end": v(6.38, 16.63) * mm});
            skLineSegment(sketch, "E419", {"start": v(13.43, 19.02) * mm, "end": v(9.98, 17.6) * mm});
            skLineSegment(sketch, "E420", {"start": v(16.67, 20.86) * mm, "end": v(13.43, 19.02) * mm});
            skLineSegment(sketch, "E421", {"start": v(19.66, 23.08) * mm, "end": v(16.67, 20.86) * mm});
            skLineSegment(sketch, "E422", {"start": v(22.35, 25.67) * mm, "end": v(19.66, 23.08) * mm});
            skLineSegment(sketch, "E423", {"start": v(24.48, 28.3) * mm, "end": v(22.35, 25.67) * mm});
            skSolve(sketch);
        }
        {
            var Q0;
            Q0=makeQuery(id+"F3.imprint","IMPRINT",FACE,{"disambiguationData":[TD([[makeQuery(id+"F3.imprint","IMPRINT",EDGE,{"derivedFrom":sQuery(id+"F3.wireOp",EDGE,"E2")}),-1.0]])]});
            var Q1;
            Q1=makeQuery(id+"F3.imprint","IMPRINT",FACE,{"disambiguationData":[TD([[makeQuery(id+"F3.imprint","IMPRINT",EDGE,{"derivedFrom":sQuery(id+"F3.wireOp",EDGE,"E89")}),-1.0]])]});
            var Q2;
            Q2=makeQuery(id+"F3.imprint","IMPRINT",FACE,{"disambiguationData":[TD([[makeQuery(id+"F3.imprint","IMPRINT",EDGE,{"derivedFrom":sQuery(id+"F3.wireOp",EDGE,"E206")}),-1.0]])]});
            var Q3;
            Q3=makeQuery(id+"F3.imprint","IMPRINT",FACE,{"disambiguationData":[TD([[makeQuery(id+"F3.imprint","IMPRINT",EDGE,{"derivedFrom":sQuery(id+"F3.wireOp",EDGE,"E386")}),-1.0]])]});
            var Q4;
            Q4=makeQuery(id+"F3.imprint","IMPRINT",FACE,{"disambiguationData":[TD([[makeQuery(id+"F3.imprint","IMPRINT",EDGE,{"derivedFrom":sQuery(id+"F3.wireOp",EDGE,"E328")}),-1.0]])]});
            extrude(context, id + "F4", {"entities" : qUnion([Q0, Q1, Q2, Q3, Q4]), "operationType" : NewBodyOperationType.REMOVE, "oppositeDirection" : true, "depth" : 1.5 * mm});
        }
        {
            var Q0;
            Q0=makeQuery(id+"F1.opExtrude","SWEPT_FACE",FACE,{"disambiguationData":[OSD([sQuery(id+"F0.wireOp",EDGE,"E1.0")])]});
            var sketch = newSketch(context, id + "F5", { "sketchPlane" : qUnion([Q0])});
            skLineSegment(sketch, "E424", {"start": v(-3.84, 79.68) * mm, "end": v(0.07, 80.04) * mm});
            skLineSegment(sketch, "E425", {"start": v(-7.66, 78.8) * mm, "end": v(-3.84, 79.68) * mm});
            skLineSegment(sketch, "E426", {"start": v(-11.33, 77.43) * mm, "end": v(-7.66, 78.8) * mm});
            skLineSegment(sketch, "E427", {"start": v(-14.79, 75.6) * mm, "end": v(-11.33, 77.43) * mm});
            skLineSegment(sketch, "E428", {"start": v(-17.98, 73.31) * mm, "end": v(-14.79, 75.6) * mm});
            skLineSegment(sketch, "E429", {"start": v(-20.84, 70.63) * mm, "end": v(-17.98, 73.31) * mm});
            skLineSegment(sketch, "E430", {"start": v(-23.32, 67.6) * mm, "end": v(-20.84, 70.63) * mm});
            skLineSegment(sketch, "E431", {"start": v(-25.38, 64.27) * mm, "end": v(-23.32, 67.6) * mm});
            skLineSegment(sketch, "E432", {"start": v(-27, 60.7) * mm, "end": v(-25.38, 64.27) * mm});
            skLineSegment(sketch, "E433", {"start": v(-28.12, 56.94) * mm, "end": v(-27, 60.7) * mm});
            skLineSegment(sketch, "E434", {"start": v(-28.74, 53.07) * mm, "end": v(-28.12, 56.94) * mm});
            skLineSegment(sketch, "E435", {"start": v(-28.84, 49.15) * mm, "end": v(-28.74, 53.07) * mm});
            skLineSegment(sketch, "E436", {"start": v(-28.43, 45.25) * mm, "end": v(-28.84, 49.15) * mm});
            skLineSegment(sketch, "E437", {"start": v(-27.51, 41.44) * mm, "end": v(-28.43, 45.25) * mm});
            skLineSegment(sketch, "E438", {"start": v(-26.18, 38) * mm, "end": v(-27.51, 41.44) * mm});
            skLineSegment(sketch, "E439", {"start": v(-25.9, 38.09) * mm, "end": v(-26.18, 38) * mm});
            skLineSegment(sketch, "E440", {"start": v(-25.68, 38.2) * mm, "end": v(-25.9, 38.09) * mm});
            skLineSegment(sketch, "E441", {"start": v(-25.5, 38.32) * mm, "end": v(-25.68, 38.2) * mm});
            skLineSegment(sketch, "E442", {"start": v(-24.8, 39.1) * mm, "end": v(-25.5, 38.32) * mm});
            skLineSegment(sketch, "E443", {"start": v(-23.6, 40.9) * mm, "end": v(-24.8, 39.1) * mm});
            skLineSegment(sketch, "E444", {"start": v(-21.99, 44.9) * mm, "end": v(-23.6, 40.9) * mm});
            skLineSegment(sketch, "E445", {"start": v(-22.53, 46.58) * mm, "end": v(-21.99, 44.9) * mm});
            skLineSegment(sketch, "E446", {"start": v(-22.84, 48.44) * mm, "end": v(-22.53, 46.58) * mm});
            skLineSegment(sketch, "E447", {"start": v(-22.86, 50.3) * mm, "end": v(-22.84, 48.44) * mm});
            skLineSegment(sketch, "E448", {"start": v(-22.86, 50.56) * mm, "end": v(-22.86, 50.3) * mm});
            skLineSegment(sketch, "E449", {"start": v(-22.86, 50.82) * mm, "end": v(-22.86, 50.56) * mm});
            skLineSegment(sketch, "E450", {"start": v(-22.84, 51.34) * mm, "end": v(-22.86, 50.82) * mm});
            skLineSegment(sketch, "E451", {"start": v(-22.77, 52.36) * mm, "end": v(-22.84, 51.34) * mm});
            skLineSegment(sketch, "E452", {"start": v(-22.61, 53.66) * mm, "end": v(-22.77, 52.36) * mm});
            skLineSegment(sketch, "E453", {"start": v(-21.89, 56.94) * mm, "end": v(-22.61, 53.66) * mm});
            skLineSegment(sketch, "E454", {"start": v(-20.7, 60.08) * mm, "end": v(-21.89, 56.94) * mm});
            skLineSegment(sketch, "E455", {"start": v(-19.06, 63.02) * mm, "end": v(-20.7, 60.08) * mm});
            skLineSegment(sketch, "E456", {"start": v(-17.02, 65.7) * mm, "end": v(-19.06, 63.02) * mm});
            skLineSegment(sketch, "E457", {"start": v(-14.62, 68.04) * mm, "end": v(-17.02, 65.7) * mm});
            skLineSegment(sketch, "E458", {"start": v(-11.9, 70.03) * mm, "end": v(-14.62, 68.04) * mm});
            skLineSegment(sketch, "E459", {"start": v(-8.93, 71.6) * mm, "end": v(-11.9, 70.03) * mm});
            skLineSegment(sketch, "E460", {"start": v(-5.76, 72.72) * mm, "end": v(-8.93, 71.6) * mm});
            skLineSegment(sketch, "E461", {"start": v(-2.47, 73.38) * mm, "end": v(-5.76, 72.72) * mm});
            skLineSegment(sketch, "E462", {"start": v(-2.38, 73.39) * mm, "end": v(-2.47, 73.38) * mm});
            skLineSegment(sketch, "E463", {"start": v(-2.3, 73.4) * mm, "end": v(-2.38, 73.39) * mm});
            skLineSegment(sketch, "E464", {"start": v(-2.13, 73.42) * mm, "end": v(-2.3, 73.4) * mm});
            skLineSegment(sketch, "E465", {"start": v(-1.8, 73.45) * mm, "end": v(-2.13, 73.42) * mm});
            skLineSegment(sketch, "E466", {"start": v(0.9, 73.56) * mm, "end": v(-1.8, 73.45) * mm});
            skLineSegment(sketch, "E467", {"start": v(4.2, 73.32) * mm, "end": v(0.9, 73.56) * mm});
            skLineSegment(sketch, "E468", {"start": v(7.44, 72.62) * mm, "end": v(4.2, 73.32) * mm});
            skLineSegment(sketch, "E469", {"start": v(10.54, 71.46) * mm, "end": v(7.44, 72.62) * mm});
            skLineSegment(sketch, "E470", {"start": v(13.46, 69.87) * mm, "end": v(10.54, 71.46) * mm});
            skLineSegment(sketch, "E471", {"start": v(16.11, 67.88) * mm, "end": v(13.46, 69.87) * mm});
            skLineSegment(sketch, "E472", {"start": v(18.46, 65.53) * mm, "end": v(16.11, 67.88) * mm});
            skLineSegment(sketch, "E473", {"start": v(20.45, 62.88) * mm, "end": v(18.46, 65.53) * mm});
            skLineSegment(sketch, "E474", {"start": v(22.04, 59.96) * mm, "end": v(20.45, 62.88) * mm});
            skLineSegment(sketch, "E475", {"start": v(23.2, 56.86) * mm, "end": v(22.04, 59.96) * mm});
            skLineSegment(sketch, "E476", {"start": v(23.9, 53.62) * mm, "end": v(23.2, 56.86) * mm});
            skLineSegment(sketch, "E477", {"start": v(23.91, 53.53) * mm, "end": v(23.9, 53.62) * mm});
            skLineSegment(sketch, "E478", {"start": v(23.92, 53.45) * mm, "end": v(23.91, 53.53) * mm});
            skLineSegment(sketch, "E479", {"start": v(23.94, 53.29) * mm, "end": v(23.92, 53.45) * mm});
            skLineSegment(sketch, "E480", {"start": v(23.99, 52.95) * mm, "end": v(23.94, 53.29) * mm});
            skLineSegment(sketch, "E481", {"start": v(24.14, 50.31) * mm, "end": v(23.99, 52.95) * mm});
            skLineSegment(sketch, "E482", {"start": v(24.12, 47.05) * mm, "end": v(24.14, 50.31) * mm});
            skLineSegment(sketch, "E483", {"start": v(24.16, 46.68) * mm, "end": v(24.12, 47.05) * mm});
            skLineSegment(sketch, "E484", {"start": v(24.26, 46.34) * mm, "end": v(24.16, 46.68) * mm});
            skLineSegment(sketch, "E485", {"start": v(24.64, 45.66) * mm, "end": v(24.26, 46.34) * mm});
            skLineSegment(sketch, "E486", {"start": v(25.1, 44.96) * mm, "end": v(24.64, 45.66) * mm});
            skLineSegment(sketch, "E487", {"start": v(25.24, 44.54) * mm, "end": v(25.1, 44.96) * mm});
            skLineSegment(sketch, "E488", {"start": v(25.32, 44.1) * mm, "end": v(25.24, 44.54) * mm});
            skLineSegment(sketch, "E489", {"start": v(25.54, 42.5) * mm, "end": v(25.32, 44.1) * mm});
            skLineSegment(sketch, "E490", {"start": v(25.8, 41.77) * mm, "end": v(25.54, 42.5) * mm});
            skLineSegment(sketch, "E491", {"start": v(25.98, 41.46) * mm, "end": v(25.8, 41.77) * mm});
            skLineSegment(sketch, "E492", {"start": v(26.2, 41.17) * mm, "end": v(25.98, 41.46) * mm});
            skLineSegment(sketch, "E493", {"start": v(26.79, 40.65) * mm, "end": v(26.2, 41.17) * mm});
            skLineSegment(sketch, "E494", {"start": v(27.46, 40.2) * mm, "end": v(26.79, 40.65) * mm});
            skLineSegment(sketch, "E495", {"start": v(28.6, 39.57) * mm, "end": v(27.46, 40.2) * mm});
            skLineSegment(sketch, "E496", {"start": v(29.73, 43.02) * mm, "end": v(28.6, 39.57) * mm});
            skLineSegment(sketch, "E497", {"start": v(30.44, 46.88) * mm, "end": v(29.73, 43.02) * mm});
            skLineSegment(sketch, "E498", {"start": v(30.63, 50.79) * mm, "end": v(30.44, 46.88) * mm});
            skLineSegment(sketch, "E499", {"start": v(30.3, 54.7) * mm, "end": v(30.63, 50.79) * mm});
            skLineSegment(sketch, "E500", {"start": v(29.48, 58.53) * mm, "end": v(30.3, 54.7) * mm});
            skLineSegment(sketch, "E501", {"start": v(28.15, 62.21) * mm, "end": v(29.48, 58.53) * mm});
            skLineSegment(sketch, "E502", {"start": v(26.35, 65.7) * mm, "end": v(28.15, 62.21) * mm});
            skLineSegment(sketch, "E503", {"start": v(24.1, 68.9) * mm, "end": v(26.35, 65.7) * mm});
            skLineSegment(sketch, "E504", {"start": v(21.46, 71.8) * mm, "end": v(24.1, 68.9) * mm});
            skLineSegment(sketch, "E505", {"start": v(18.45, 74.32) * mm, "end": v(21.46, 71.8) * mm});
            skLineSegment(sketch, "E506", {"start": v(15.14, 76.42) * mm, "end": v(18.45, 74.32) * mm});
            skLineSegment(sketch, "E507", {"start": v(11.59, 78.06) * mm, "end": v(15.14, 76.42) * mm});
            skLineSegment(sketch, "E508", {"start": v(7.84, 79.23) * mm, "end": v(11.59, 78.06) * mm});
            skLineSegment(sketch, "E509", {"start": v(3.98, 79.9) * mm, "end": v(7.84, 79.23) * mm});
            skLineSegment(sketch, "E510", {"start": v(0.07, 80.04) * mm, "end": v(3.98, 79.9) * mm});
            skLineSegment(sketch, "E511", {"start": v(7.13, 37.5) * mm, "end": v(7.14, 37.44) * mm});
            skLineSegment(sketch, "E512", {"start": v(7.11, 37.54) * mm, "end": v(7.13, 37.5) * mm});
            skLineSegment(sketch, "E513", {"start": v(7.08, 37.65) * mm, "end": v(7.11, 37.54) * mm});
            skLineSegment(sketch, "E514", {"start": v(7.02, 37.86) * mm, "end": v(7.08, 37.65) * mm});
            skLineSegment(sketch, "E515", {"start": v(6.14, 40.62) * mm, "end": v(7.02, 37.86) * mm});
            skLineSegment(sketch, "E516", {"start": v(4.96, 43.76) * mm, "end": v(6.14, 40.62) * mm});
            skLineSegment(sketch, "E517", {"start": v(4.52, 45.4) * mm, "end": v(4.96, 43.76) * mm});
            skLineSegment(sketch, "E518", {"start": v(4.4, 46.27) * mm, "end": v(4.52, 45.4) * mm});
            skLineSegment(sketch, "E519", {"start": v(4.4, 47.15) * mm, "end": v(4.4, 46.27) * mm});
            skLineSegment(sketch, "E520", {"start": v(4.53, 48.01) * mm, "end": v(4.4, 47.15) * mm});
            skLineSegment(sketch, "E521", {"start": v(4.77, 48.85) * mm, "end": v(4.53, 48.01) * mm});
            skLineSegment(sketch, "E522", {"start": v(5.45, 50.43) * mm, "end": v(4.77, 48.85) * mm});
            skLineSegment(sketch, "E523", {"start": v(6.04, 51.26) * mm, "end": v(5.45, 50.43) * mm});
            skLineSegment(sketch, "E524", {"start": v(6.06, 51.32) * mm, "end": v(6.04, 51.26) * mm});
            skLineSegment(sketch, "E525", {"start": v(6.06, 51.4) * mm, "end": v(6.06, 51.32) * mm});
            skLineSegment(sketch, "E526", {"start": v(6.04, 51.62) * mm, "end": v(6.06, 51.4) * mm});
            skLineSegment(sketch, "E527", {"start": v(6.01, 51.87) * mm, "end": v(6.04, 51.62) * mm});
            skLineSegment(sketch, "E528", {"start": v(5.98, 51.96) * mm, "end": v(6.01, 51.87) * mm});
            skLineSegment(sketch, "E529", {"start": v(5.96, 52) * mm, "end": v(5.98, 51.96) * mm});
            skLineSegment(sketch, "E530", {"start": v(4.63, 53.53) * mm, "end": v(5.96, 52) * mm});
            skLineSegment(sketch, "E531", {"start": v(4.47, 53.68) * mm, "end": v(4.63, 53.53) * mm});
            skLineSegment(sketch, "E532", {"start": v(4.3, 53.8) * mm, "end": v(4.47, 53.68) * mm});
            skLineSegment(sketch, "E533", {"start": v(4.1, 53.87) * mm, "end": v(4.3, 53.8) * mm});
            skLineSegment(sketch, "E534", {"start": v(3.91, 53.89) * mm, "end": v(4.1, 53.87) * mm});
            skLineSegment(sketch, "E535", {"start": v(3.45, 53.82) * mm, "end": v(3.91, 53.89) * mm});
            skLineSegment(sketch, "E536", {"start": v(3.24, 53.76) * mm, "end": v(3.45, 53.82) * mm});
            skLineSegment(sketch, "E537", {"start": v(3.06, 53.67) * mm, "end": v(3.24, 53.76) * mm});
            skLineSegment(sketch, "E538", {"start": v(1.35, 52.14) * mm, "end": v(3.06, 53.67) * mm});
            skLineSegment(sketch, "E539", {"start": v(0.68, 53.03) * mm, "end": v(1.35, 52.14) * mm});
            skLineSegment(sketch, "E540", {"start": v(-1.23, 55.71) * mm, "end": v(0.68, 53.03) * mm});
            skLineSegment(sketch, "E541", {"start": v(-2.98, 58.5) * mm, "end": v(-1.23, 55.71) * mm});
            skLineSegment(sketch, "E542", {"start": v(-2.98, 58.5) * mm, "end": v(-4.65, 61.35) * mm});
            skLineSegment(sketch, "E543", {"start": v(-4.65, 61.35) * mm, "end": v(-6.07, 64.16) * mm});
            skLineSegment(sketch, "E544", {"start": v(-15.99, 64.45) * mm, "end": v(-6.07, 64.16) * mm});
            skLineSegment(sketch, "E545", {"start": v(-16.9, 63.16) * mm, "end": v(-15.99, 64.45) * mm});
            skLineSegment(sketch, "E546", {"start": v(-17.14, 62.82) * mm, "end": v(-16.9, 63.16) * mm});
            skLineSegment(sketch, "E547", {"start": v(-17.08, 62.75) * mm, "end": v(-17.14, 62.82) * mm});
            skLineSegment(sketch, "E548", {"start": v(-16.77, 62.48) * mm, "end": v(-17.08, 62.75) * mm});
            skLineSegment(sketch, "E549", {"start": v(-16.63, 62.4) * mm, "end": v(-16.77, 62.48) * mm});
            skLineSegment(sketch, "E550", {"start": v(-16.48, 62.34) * mm, "end": v(-16.63, 62.4) * mm});
            skLineSegment(sketch, "E551", {"start": v(-15.64, 62.23) * mm, "end": v(-16.48, 62.34) * mm});
            skLineSegment(sketch, "E552", {"start": v(-14.8, 61.94) * mm, "end": v(-15.64, 62.23) * mm});
            skLineSegment(sketch, "E553", {"start": v(-14.37, 61.73) * mm, "end": v(-14.8, 61.94) * mm});
            skLineSegment(sketch, "E554", {"start": v(-14.14, 61.61) * mm, "end": v(-14.37, 61.73) * mm});
            skLineSegment(sketch, "E555", {"start": v(-13.93, 61.45) * mm, "end": v(-14.14, 61.61) * mm});
            skLineSegment(sketch, "E556", {"start": v(-13.83, 61.33) * mm, "end": v(-13.93, 61.45) * mm});
            skLineSegment(sketch, "E557", {"start": v(-13.75, 61.2) * mm, "end": v(-13.83, 61.33) * mm});
            skLineSegment(sketch, "E558", {"start": v(-13.71, 61.05) * mm, "end": v(-13.75, 61.2) * mm});
            skLineSegment(sketch, "E559", {"start": v(-13.7, 60.9) * mm, "end": v(-13.71, 61.05) * mm});
            skLineSegment(sketch, "E560", {"start": v(-13.74, 60.41) * mm, "end": v(-13.7, 60.9) * mm});
            skLineSegment(sketch, "E561", {"start": v(-14.1, 58.7) * mm, "end": v(-13.74, 60.41) * mm});
            skLineSegment(sketch, "E562", {"start": v(-14.73, 57.08) * mm, "end": v(-14.1, 58.7) * mm});
            skLineSegment(sketch, "E563", {"start": v(-15.35, 55.48) * mm, "end": v(-14.73, 57.08) * mm});
            skLineSegment(sketch, "E564", {"start": v(-15.49, 55.08) * mm, "end": v(-15.35, 55.48) * mm});
            skLineSegment(sketch, "E565", {"start": v(-15.57, 54.7) * mm, "end": v(-15.49, 55.08) * mm});
            skLineSegment(sketch, "E566", {"start": v(-15.56, 54.55) * mm, "end": v(-15.57, 54.7) * mm});
            skLineSegment(sketch, "E567", {"start": v(-15.52, 54.4) * mm, "end": v(-15.56, 54.55) * mm});
            skLineSegment(sketch, "E568", {"start": v(-15.43, 54.26) * mm, "end": v(-15.52, 54.4) * mm});
            skLineSegment(sketch, "E569", {"start": v(-15.32, 54.14) * mm, "end": v(-15.43, 54.26) * mm});
            skLineSegment(sketch, "E570", {"start": v(-15.18, 54.04) * mm, "end": v(-15.32, 54.14) * mm});
            skLineSegment(sketch, "E571", {"start": v(-15.02, 53.96) * mm, "end": v(-15.18, 54.04) * mm});
            skLineSegment(sketch, "E572", {"start": v(-14.62, 53.8) * mm, "end": v(-15.02, 53.96) * mm});
            skLineSegment(sketch, "E573", {"start": v(-13.83, 53.45) * mm, "end": v(-14.62, 53.8) * mm});
            skLineSegment(sketch, "E574", {"start": v(-13.04, 53.04) * mm, "end": v(-13.83, 53.45) * mm});
            skLineSegment(sketch, "E575", {"start": v(-12.87, 52.97) * mm, "end": v(-13.04, 53.04) * mm});
            skLineSegment(sketch, "E576", {"start": v(-12.7, 52.94) * mm, "end": v(-12.87, 52.97) * mm});
            skLineSegment(sketch, "E577", {"start": v(-12.64, 52.94) * mm, "end": v(-12.7, 52.94) * mm});
            skLineSegment(sketch, "E578", {"start": v(-12.58, 52.95) * mm, "end": v(-12.64, 52.94) * mm});
            skLineSegment(sketch, "E579", {"start": v(-12.43, 53) * mm, "end": v(-12.58, 52.95) * mm});
            skLineSegment(sketch, "E580", {"start": v(-12.28, 53.08) * mm, "end": v(-12.43, 53) * mm});
            skLineSegment(sketch, "E581", {"start": v(-12.15, 53.2) * mm, "end": v(-12.28, 53.08) * mm});
            skLineSegment(sketch, "E582", {"start": v(-11.91, 53.5) * mm, "end": v(-12.15, 53.2) * mm});
            skLineSegment(sketch, "E583", {"start": v(-11.54, 54.24) * mm, "end": v(-11.91, 53.5) * mm});
            skLineSegment(sketch, "E584", {"start": v(-11.18, 55.07) * mm, "end": v(-11.54, 54.24) * mm});
            skLineSegment(sketch, "E585", {"start": v(-11.08, 55.3) * mm, "end": v(-11.18, 55.07) * mm});
            skLineSegment(sketch, "E586", {"start": v(-11, 55.42) * mm, "end": v(-11.08, 55.3) * mm});
            skLineSegment(sketch, "E587", {"start": v(-10.9, 55.53) * mm, "end": v(-11, 55.42) * mm});
            skLineSegment(sketch, "E588", {"start": v(-10.77, 55.61) * mm, "end": v(-10.9, 55.53) * mm});
            skLineSegment(sketch, "E589", {"start": v(-10.62, 55.67) * mm, "end": v(-10.77, 55.61) * mm});
            skLineSegment(sketch, "E590", {"start": v(-10.46, 55.68) * mm, "end": v(-10.62, 55.67) * mm});
            skLineSegment(sketch, "E591", {"start": v(-10.31, 55.68) * mm, "end": v(-10.46, 55.68) * mm});
            skLineSegment(sketch, "E592", {"start": v(-10.05, 55.62) * mm, "end": v(-10.31, 55.68) * mm});
            skLineSegment(sketch, "E593", {"start": v(-9.8, 55.52) * mm, "end": v(-10.05, 55.62) * mm});
            skLineSegment(sketch, "E594", {"start": v(-9.41, 55.28) * mm, "end": v(-9.8, 55.52) * mm});
            skLineSegment(sketch, "E595", {"start": v(-9.41, 55.28) * mm, "end": v(-8.71, 54.72) * mm});
            skLineSegment(sketch, "E596", {"start": v(-8.71, 54.72) * mm, "end": v(-7.52, 53.41) * mm});
            skLineSegment(sketch, "E597", {"start": v(-5.75, 50.43) * mm, "end": v(-7.52, 53.41) * mm});
            skLineSegment(sketch, "E598", {"start": v(-4.5, 48.05) * mm, "end": v(-5.75, 50.43) * mm});
            skLineSegment(sketch, "E599", {"start": v(-3.4, 45.6) * mm, "end": v(-4.5, 48.05) * mm});
            skLineSegment(sketch, "E600", {"start": v(-1.9, 40.46) * mm, "end": v(-3.4, 45.6) * mm});
            skLineSegment(sketch, "E601", {"start": v(-1.27, 37.87) * mm, "end": v(-1.9, 40.46) * mm});
            skLineSegment(sketch, "E602", {"start": v(-0.76, 35.22) * mm, "end": v(-1.27, 37.87) * mm});
            skLineSegment(sketch, "E603", {"start": v(-0.7, 34.51) * mm, "end": v(-0.76, 35.22) * mm});
            skLineSegment(sketch, "E604", {"start": v(-0.78, 33.82) * mm, "end": v(-0.7, 34.51) * mm});
            skLineSegment(sketch, "E605", {"start": v(-0.94, 33.14) * mm, "end": v(-0.78, 33.82) * mm});
            skLineSegment(sketch, "E606", {"start": v(-1, 32.95) * mm, "end": v(-0.94, 33.14) * mm});
            skLineSegment(sketch, "E607", {"start": v(-1.1, 32.79) * mm, "end": v(-1, 32.95) * mm});
            skLineSegment(sketch, "E608", {"start": v(-1.12, 32.74) * mm, "end": v(-1.1, 32.79) * mm});
            skLineSegment(sketch, "E609", {"start": v(-1, 32.7) * mm, "end": v(-1.12, 32.74) * mm});
            skLineSegment(sketch, "E610", {"start": v(-0.64, 32.56) * mm, "end": v(-1, 32.7) * mm});
            skLineSegment(sketch, "E611", {"start": v(-0.08, 32.2) * mm, "end": v(-0.64, 32.56) * mm});
            skLineSegment(sketch, "E612", {"start": v(0.5, 31.87) * mm, "end": v(-0.08, 32.2) * mm});
            skLineSegment(sketch, "E613", {"start": v(0.8, 31.65) * mm, "end": v(0.5, 31.87) * mm});
            skLineSegment(sketch, "E614", {"start": v(0.9, 31.53) * mm, "end": v(0.8, 31.65) * mm});
            skLineSegment(sketch, "E615", {"start": v(1.06, 31.92) * mm, "end": v(0.9, 31.53) * mm});
            skLineSegment(sketch, "E616", {"start": v(1.37, 32.42) * mm, "end": v(1.06, 31.92) * mm});
            skLineSegment(sketch, "E617", {"start": v(2.14, 33.22) * mm, "end": v(1.37, 32.42) * mm});
            skLineSegment(sketch, "E618", {"start": v(3.66, 34.76) * mm, "end": v(2.14, 33.22) * mm});
            skLineSegment(sketch, "E619", {"start": v(4.46, 35.52) * mm, "end": v(3.66, 34.76) * mm});
            skLineSegment(sketch, "E620", {"start": v(5.38, 36.12) * mm, "end": v(4.46, 35.52) * mm});
            skLineSegment(sketch, "E621", {"start": v(6.34, 36.7) * mm, "end": v(5.38, 36.12) * mm});
            skLineSegment(sketch, "E622", {"start": v(6.6, 36.82) * mm, "end": v(6.34, 36.7) * mm});
            skLineSegment(sketch, "E623", {"start": v(6.9, 36.92) * mm, "end": v(6.6, 36.82) * mm});
            skLineSegment(sketch, "E624", {"start": v(7.2, 36.96) * mm, "end": v(6.9, 36.92) * mm});
            skLineSegment(sketch, "E625", {"start": v(7.24, 36.96) * mm, "end": v(7.2, 36.96) * mm});
            skLineSegment(sketch, "E626", {"start": v(7.24, 37.08) * mm, "end": v(7.24, 36.96) * mm});
            skLineSegment(sketch, "E627", {"start": v(7.14, 37.44) * mm, "end": v(7.24, 37.08) * mm});
            skLineSegment(sketch, "E628", {"start": v(19.26, 51.6) * mm, "end": v(19.9, 50.2) * mm});
            skLineSegment(sketch, "E629", {"start": v(16.7, 56.88) * mm, "end": v(19.26, 51.6) * mm});
            skLineSegment(sketch, "E630", {"start": v(15.63, 59.63) * mm, "end": v(16.7, 56.88) * mm});
            skLineSegment(sketch, "E631", {"start": v(15.42, 60.37) * mm, "end": v(15.63, 59.63) * mm});
            skLineSegment(sketch, "E632", {"start": v(15.34, 61.14) * mm, "end": v(15.42, 60.37) * mm});
            skLineSegment(sketch, "E633", {"start": v(15.4, 62.63) * mm, "end": v(15.34, 61.14) * mm});
            skLineSegment(sketch, "E634", {"start": v(15.54, 64.07) * mm, "end": v(15.4, 62.63) * mm});
            skLineSegment(sketch, "E635", {"start": v(15.54, 64.24) * mm, "end": v(15.54, 64.07) * mm});
            skLineSegment(sketch, "E636", {"start": v(15.52, 64.4) * mm, "end": v(15.54, 64.24) * mm});
            skLineSegment(sketch, "E637", {"start": v(15.5, 64.44) * mm, "end": v(15.52, 64.4) * mm});
            skLineSegment(sketch, "E638", {"start": v(15.46, 64.47) * mm, "end": v(15.5, 64.44) * mm});
            skLineSegment(sketch, "E639", {"start": v(15.42, 64.5) * mm, "end": v(15.46, 64.47) * mm});
            skLineSegment(sketch, "E640", {"start": v(14.78, 64.86) * mm, "end": v(15.42, 64.5) * mm});
            skLineSegment(sketch, "E641", {"start": v(14.47, 65.04) * mm, "end": v(14.78, 64.86) * mm});
            skLineSegment(sketch, "E642", {"start": v(14.42, 65.06) * mm, "end": v(14.47, 65.04) * mm});
            skLineSegment(sketch, "E643", {"start": v(14.38, 65.07) * mm, "end": v(14.42, 65.06) * mm});
            skLineSegment(sketch, "E644", {"start": v(14.34, 65.07) * mm, "end": v(14.38, 65.07) * mm});
            skLineSegment(sketch, "E645", {"start": v(14.3, 65.07) * mm, "end": v(14.34, 65.07) * mm});
            skLineSegment(sketch, "E646", {"start": v(13.59, 64.82) * mm, "end": v(14.3, 65.07) * mm});
            skLineSegment(sketch, "E647", {"start": v(12.13, 64.55) * mm, "end": v(13.59, 64.82) * mm});
            skLineSegment(sketch, "E648", {"start": v(10.63, 64.46) * mm, "end": v(12.13, 64.55) * mm});
            skLineSegment(sketch, "E649", {"start": v(9.15, 64.6) * mm, "end": v(10.63, 64.46) * mm});
            skLineSegment(sketch, "E650", {"start": v(7.67, 64.72) * mm, "end": v(9.15, 64.6) * mm});
            skLineSegment(sketch, "E651", {"start": v(6.25, 65.14) * mm, "end": v(7.67, 64.72) * mm});
            skLineSegment(sketch, "E652", {"start": v(6.1, 65.17) * mm, "end": v(6.25, 65.14) * mm});
            skLineSegment(sketch, "E653", {"start": v(5.97, 65.17) * mm, "end": v(6.1, 65.17) * mm});
            skLineSegment(sketch, "E654", {"start": v(5.94, 65.16) * mm, "end": v(5.97, 65.17) * mm});
            skLineSegment(sketch, "E655", {"start": v(5.9, 65.14) * mm, "end": v(5.94, 65.16) * mm});
            skLineSegment(sketch, "E656", {"start": v(5.8, 65.07) * mm, "end": v(5.9, 65.14) * mm});
            skLineSegment(sketch, "E657", {"start": v(5.32, 64.53) * mm, "end": v(5.8, 65.07) * mm});
            skLineSegment(sketch, "E658", {"start": v(4.86, 63.99) * mm, "end": v(5.32, 64.53) * mm});
            skLineSegment(sketch, "E659", {"start": v(4.69, 63.72) * mm, "end": v(4.86, 63.99) * mm});
            skLineSegment(sketch, "E660", {"start": v(4.64, 63.59) * mm, "end": v(4.69, 63.72) * mm});
            skLineSegment(sketch, "E661", {"start": v(4.62, 63.45) * mm, "end": v(4.64, 63.59) * mm});
            skLineSegment(sketch, "E662", {"start": v(4.62, 63.4) * mm, "end": v(4.62, 63.45) * mm});
            skLineSegment(sketch, "E663", {"start": v(4.65, 63.37) * mm, "end": v(4.62, 63.4) * mm});
            skLineSegment(sketch, "E664", {"start": v(4.77, 63.3) * mm, "end": v(4.65, 63.37) * mm});
            skLineSegment(sketch, "E665", {"start": v(4.96, 63.25) * mm, "end": v(4.77, 63.3) * mm});
            skLineSegment(sketch, "E666", {"start": v(5.71, 62.96) * mm, "end": v(4.96, 63.25) * mm});
            skLineSegment(sketch, "E667", {"start": v(7, 62.28) * mm, "end": v(5.71, 62.96) * mm});
            skLineSegment(sketch, "E668", {"start": v(7.62, 61.9) * mm, "end": v(7, 62.28) * mm});
            skLineSegment(sketch, "E669", {"start": v(7.94, 61.67) * mm, "end": v(7.62, 61.9) * mm});
            skLineSegment(sketch, "E670", {"start": v(8.25, 61.4) * mm, "end": v(7.94, 61.67) * mm});
            skLineSegment(sketch, "E671", {"start": v(8.5, 61.06) * mm, "end": v(8.25, 61.4) * mm});
            skLineSegment(sketch, "E672", {"start": v(8.66, 60.68) * mm, "end": v(8.5, 61.06) * mm});
            skLineSegment(sketch, "E673", {"start": v(8.72, 60.45) * mm, "end": v(8.66, 60.68) * mm});
            skLineSegment(sketch, "E674", {"start": v(8.74, 60.22) * mm, "end": v(8.72, 60.45) * mm});
            skLineSegment(sketch, "E675", {"start": v(8.7, 60) * mm, "end": v(8.74, 60.22) * mm});
            skLineSegment(sketch, "E676", {"start": v(8.62, 59.78) * mm, "end": v(8.7, 60) * mm});
            skLineSegment(sketch, "E677", {"start": v(7.72, 58.54) * mm, "end": v(8.62, 59.78) * mm});
            skLineSegment(sketch, "E678", {"start": v(7.01, 57.28) * mm, "end": v(7.72, 58.54) * mm});
            skLineSegment(sketch, "E679", {"start": v(6.57, 56.65) * mm, "end": v(7.01, 57.28) * mm});
            skLineSegment(sketch, "E680", {"start": v(6, 56.1) * mm, "end": v(6.57, 56.65) * mm});
            skLineSegment(sketch, "E681", {"start": v(5.72, 55.86) * mm, "end": v(6, 56.1) * mm});
            skLineSegment(sketch, "E682", {"start": v(5.63, 55.75) * mm, "end": v(5.72, 55.86) * mm});
            skLineSegment(sketch, "E683", {"start": v(5.56, 55.64) * mm, "end": v(5.63, 55.75) * mm});
            skLineSegment(sketch, "E684", {"start": v(5.53, 55.52) * mm, "end": v(5.56, 55.64) * mm});
            skLineSegment(sketch, "E685", {"start": v(5.52, 55.4) * mm, "end": v(5.53, 55.52) * mm});
            skLineSegment(sketch, "E686", {"start": v(5.53, 55.26) * mm, "end": v(5.52, 55.4) * mm});
            skLineSegment(sketch, "E687", {"start": v(5.57, 55.13) * mm, "end": v(5.53, 55.26) * mm});
            skLineSegment(sketch, "E688", {"start": v(5.73, 54.84) * mm, "end": v(5.57, 55.13) * mm});
            skLineSegment(sketch, "E689", {"start": v(5.93, 54.56) * mm, "end": v(5.73, 54.84) * mm});
            skLineSegment(sketch, "E690", {"start": v(6.38, 54.01) * mm, "end": v(5.93, 54.56) * mm});
            skLineSegment(sketch, "E691", {"start": v(6.87, 53.47) * mm, "end": v(6.38, 54.01) * mm});
            skLineSegment(sketch, "E692", {"start": v(7.12, 53.22) * mm, "end": v(6.87, 53.47) * mm});
            skLineSegment(sketch, "E693", {"start": v(7.24, 53.12) * mm, "end": v(7.12, 53.22) * mm});
            skLineSegment(sketch, "E694", {"start": v(7.36, 53.05) * mm, "end": v(7.24, 53.12) * mm});
            skLineSegment(sketch, "E695", {"start": v(7.49, 53) * mm, "end": v(7.36, 53.05) * mm});
            skLineSegment(sketch, "E696", {"start": v(7.64, 52.97) * mm, "end": v(7.49, 53) * mm});
            skLineSegment(sketch, "E697", {"start": v(7.98, 52.93) * mm, "end": v(7.64, 52.97) * mm});
            skLineSegment(sketch, "E698", {"start": v(8.03, 52.93) * mm, "end": v(7.98, 52.93) * mm});
            skLineSegment(sketch, "E699", {"start": v(8.08, 52.94) * mm, "end": v(8.03, 52.93) * mm});
            skLineSegment(sketch, "E700", {"start": v(8.12, 52.95) * mm, "end": v(8.08, 52.94) * mm});
            skLineSegment(sketch, "E701", {"start": v(8.16, 52.98) * mm, "end": v(8.12, 52.95) * mm});
            skLineSegment(sketch, "E702", {"start": v(8.44, 53.21) * mm, "end": v(8.16, 52.98) * mm});
            skLineSegment(sketch, "E703", {"start": v(8.78, 53.44) * mm, "end": v(8.44, 53.21) * mm});
            skLineSegment(sketch, "E704", {"start": v(9, 53.52) * mm, "end": v(8.78, 53.44) * mm});
            skLineSegment(sketch, "E705", {"start": v(9.13, 53.55) * mm, "end": v(9, 53.52) * mm});
            skLineSegment(sketch, "E706", {"start": v(9.26, 53.56) * mm, "end": v(9.13, 53.55) * mm});
            skLineSegment(sketch, "E707", {"start": v(9.4, 53.54) * mm, "end": v(9.26, 53.56) * mm});
            skLineSegment(sketch, "E708", {"start": v(9.53, 53.5) * mm, "end": v(9.4, 53.54) * mm});
            skLineSegment(sketch, "E709", {"start": v(9.74, 53.39) * mm, "end": v(9.53, 53.5) * mm});
            skLineSegment(sketch, "E710", {"start": v(9.92, 53.23) * mm, "end": v(9.74, 53.39) * mm});
            skLineSegment(sketch, "E711", {"start": v(10.07, 53.06) * mm, "end": v(9.92, 53.23) * mm});
            skLineSegment(sketch, "E712", {"start": v(11.42, 50.41) * mm, "end": v(10.07, 53.06) * mm});
            skLineSegment(sketch, "E713", {"start": v(15.28, 41.47) * mm, "end": v(11.42, 50.41) * mm});
            skLineSegment(sketch, "E714", {"start": v(15.64, 40.26) * mm, "end": v(15.28, 41.47) * mm});
            skLineSegment(sketch, "E715", {"start": v(15.67, 39.91) * mm, "end": v(15.64, 40.26) * mm});
            skLineSegment(sketch, "E716", {"start": v(15.64, 39.57) * mm, "end": v(15.67, 39.91) * mm});
            skLineSegment(sketch, "E717", {"start": v(15.56, 39.24) * mm, "end": v(15.64, 39.57) * mm});
            skLineSegment(sketch, "E718", {"start": v(15.44, 38.92) * mm, "end": v(15.56, 39.24) * mm});
            skLineSegment(sketch, "E719", {"start": v(15.12, 38.36) * mm, "end": v(15.44, 38.92) * mm});
            skLineSegment(sketch, "E720", {"start": v(14.71, 37.86) * mm, "end": v(15.12, 38.36) * mm});
            skLineSegment(sketch, "E721", {"start": v(13.83, 36.97) * mm, "end": v(14.71, 37.86) * mm});
            skLineSegment(sketch, "E722", {"start": v(12.06, 35.36) * mm, "end": v(13.83, 36.97) * mm});
            skLineSegment(sketch, "E723", {"start": v(11.85, 35.14) * mm, "end": v(12.06, 35.36) * mm});
            skLineSegment(sketch, "E724", {"start": v(11.75, 35.03) * mm, "end": v(11.85, 35.14) * mm});
            skLineSegment(sketch, "E725", {"start": v(11.7, 34.96) * mm, "end": v(11.75, 35.03) * mm});
            skLineSegment(sketch, "E726", {"start": v(11.92, 34.74) * mm, "end": v(11.7, 34.96) * mm});
            skLineSegment(sketch, "E727", {"start": v(12.4, 34.27) * mm, "end": v(11.92, 34.74) * mm});
            skLineSegment(sketch, "E728", {"start": v(12.73, 33.81) * mm, "end": v(12.4, 34.27) * mm});
            skLineSegment(sketch, "E729", {"start": v(13, 33.61) * mm, "end": v(12.73, 33.81) * mm});
            skLineSegment(sketch, "E730", {"start": v(14.12, 34.32) * mm, "end": v(13, 33.61) * mm});
            skLineSegment(sketch, "E731", {"start": v(15.51, 34.9) * mm, "end": v(14.12, 34.32) * mm});
            skLineSegment(sketch, "E732", {"start": v(16.94, 35.38) * mm, "end": v(15.51, 34.9) * mm});
            skLineSegment(sketch, "E733", {"start": v(18.41, 35.7) * mm, "end": v(16.94, 35.38) * mm});
            skLineSegment(sketch, "E734", {"start": v(20.45, 35.86) * mm, "end": v(18.41, 35.7) * mm});
            skLineSegment(sketch, "E735", {"start": v(22.5, 35.84) * mm, "end": v(20.45, 35.86) * mm});
            skLineSegment(sketch, "E736", {"start": v(24.51, 35.36) * mm, "end": v(22.5, 35.84) * mm});
            skLineSegment(sketch, "E737", {"start": v(26.23, 34.74) * mm, "end": v(24.51, 35.36) * mm});
            skLineSegment(sketch, "E738", {"start": v(26.53, 35.22) * mm, "end": v(26.23, 34.74) * mm});
            skLineSegment(sketch, "E739", {"start": v(26.9, 35.89) * mm, "end": v(26.53, 35.22) * mm});
            skLineSegment(sketch, "E740", {"start": v(27.15, 36.34) * mm, "end": v(26.9, 35.89) * mm});
            skLineSegment(sketch, "E741", {"start": v(26.61, 36.62) * mm, "end": v(27.15, 36.34) * mm});
            skLineSegment(sketch, "E742", {"start": v(25.92, 37.17) * mm, "end": v(26.61, 36.62) * mm});
            skLineSegment(sketch, "E743", {"start": v(24.83, 38.49) * mm, "end": v(25.92, 37.17) * mm});
            skLineSegment(sketch, "E744", {"start": v(23.85, 39.9) * mm, "end": v(24.83, 38.49) * mm});
            skLineSegment(sketch, "E745", {"start": v(23.53, 40.71) * mm, "end": v(23.85, 39.9) * mm});
            skLineSegment(sketch, "E746", {"start": v(23.34, 41.54) * mm, "end": v(23.53, 40.71) * mm});
            skLineSegment(sketch, "E747", {"start": v(22.68, 43.62) * mm, "end": v(23.34, 41.54) * mm});
            skLineSegment(sketch, "E748", {"start": v(21.76, 46.01) * mm, "end": v(22.68, 43.62) * mm});
            skLineSegment(sketch, "E749", {"start": v(19.9, 50.2) * mm, "end": v(21.76, 46.01) * mm});
            skLineSegment(sketch, "E750", {"start": v(-24.75, 35.3) * mm, "end": v(-24.63, 35.34) * mm});
            skLineSegment(sketch, "E751", {"start": v(-24.8, 35.27) * mm, "end": v(-24.75, 35.3) * mm});
            skLineSegment(sketch, "E752", {"start": v(-24.43, 34.33) * mm, "end": v(-24.8, 35.27) * mm});
            skLineSegment(sketch, "E753", {"start": v(-23.98, 33.69) * mm, "end": v(-24.43, 34.33) * mm});
            skLineSegment(sketch, "E754", {"start": v(-23.7, 33.94) * mm, "end": v(-23.98, 33.69) * mm});
            skLineSegment(sketch, "E755", {"start": v(-23.27, 34.2) * mm, "end": v(-23.7, 33.94) * mm});
            skLineSegment(sketch, "E756", {"start": v(-22.42, 34.73) * mm, "end": v(-23.27, 34.2) * mm});
            skLineSegment(sketch, "E757", {"start": v(-20.56, 35.4) * mm, "end": v(-22.42, 34.73) * mm});
            skLineSegment(sketch, "E758", {"start": v(-19.58, 35.62) * mm, "end": v(-20.56, 35.4) * mm});
            skLineSegment(sketch, "E759", {"start": v(-18.59, 35.67) * mm, "end": v(-19.58, 35.62) * mm});
            skLineSegment(sketch, "E760", {"start": v(-16.63, 35.66) * mm, "end": v(-18.59, 35.67) * mm});
            skLineSegment(sketch, "E761", {"start": v(-14.46, 35.48) * mm, "end": v(-16.63, 35.66) * mm});
            skLineSegment(sketch, "E762", {"start": v(-14.46, 36.23) * mm, "end": v(-14.46, 35.48) * mm});
            skLineSegment(sketch, "E763", {"start": v(-14.49, 36.46) * mm, "end": v(-14.46, 36.23) * mm});
            skLineSegment(sketch, "E764", {"start": v(-14.51, 36.54) * mm, "end": v(-14.49, 36.46) * mm});
            skLineSegment(sketch, "E765", {"start": v(-14.55, 36.61) * mm, "end": v(-14.51, 36.54) * mm});
            skLineSegment(sketch, "E766", {"start": v(-14.6, 36.68) * mm, "end": v(-14.55, 36.61) * mm});
            skLineSegment(sketch, "E767", {"start": v(-14.68, 36.74) * mm, "end": v(-14.6, 36.68) * mm});
            skLineSegment(sketch, "E768", {"start": v(-14.88, 36.87) * mm, "end": v(-14.68, 36.74) * mm});
            skLineSegment(sketch, "E769", {"start": v(-15.82, 37.38) * mm, "end": v(-14.88, 36.87) * mm});
            skLineSegment(sketch, "E770", {"start": v(-16.22, 37.83) * mm, "end": v(-15.82, 37.38) * mm});
            skLineSegment(sketch, "E771", {"start": v(-16.5, 38.34) * mm, "end": v(-16.22, 37.83) * mm});
            skLineSegment(sketch, "E772", {"start": v(-16.7, 38.88) * mm, "end": v(-16.5, 38.34) * mm});
            skLineSegment(sketch, "E773", {"start": v(-16.77, 39.46) * mm, "end": v(-16.7, 38.88) * mm});
            skLineSegment(sketch, "E774", {"start": v(-16.62, 40.54) * mm, "end": v(-16.77, 39.46) * mm});
            skLineSegment(sketch, "E775", {"start": v(-16.01, 42.57) * mm, "end": v(-16.62, 40.54) * mm});
            skLineSegment(sketch, "E776", {"start": v(-14.67, 46.54) * mm, "end": v(-16.01, 42.57) * mm});
            skLineSegment(sketch, "E777", {"start": v(-13.09, 50.36) * mm, "end": v(-14.67, 46.54) * mm});
            skLineSegment(sketch, "E778", {"start": v(-13.07, 50.75) * mm, "end": v(-13.09, 50.36) * mm});
            skLineSegment(sketch, "E779", {"start": v(-13.1, 50.91) * mm, "end": v(-13.07, 50.75) * mm});
            skLineSegment(sketch, "E780", {"start": v(-13.12, 50.96) * mm, "end": v(-13.1, 50.91) * mm});
            skLineSegment(sketch, "E781", {"start": v(-13.15, 51) * mm, "end": v(-13.12, 50.96) * mm});
            skLineSegment(sketch, "E782", {"start": v(-13.28, 51.12) * mm, "end": v(-13.15, 51) * mm});
            skLineSegment(sketch, "E783", {"start": v(-13.46, 51.24) * mm, "end": v(-13.28, 51.12) * mm});
            skLineSegment(sketch, "E784", {"start": v(-13.85, 51.47) * mm, "end": v(-13.46, 51.24) * mm});
            skLineSegment(sketch, "E785", {"start": v(-13.98, 51.55) * mm, "end": v(-13.85, 51.47) * mm});
            skLineSegment(sketch, "E786", {"start": v(-14.11, 51.63) * mm, "end": v(-13.98, 51.55) * mm});
            skLineSegment(sketch, "E787", {"start": v(-14.38, 51.78) * mm, "end": v(-14.11, 51.63) * mm});
            skLineSegment(sketch, "E788", {"start": v(-14.94, 52.05) * mm, "end": v(-14.38, 51.78) * mm});
            skLineSegment(sketch, "E789", {"start": v(-15.4, 52.25) * mm, "end": v(-14.94, 52.05) * mm});
            skLineSegment(sketch, "E790", {"start": v(-15.8, 52.4) * mm, "end": v(-15.4, 52.25) * mm});
            skLineSegment(sketch, "E791", {"start": v(-15.87, 52.41) * mm, "end": v(-15.8, 52.4) * mm});
            skLineSegment(sketch, "E792", {"start": v(-15.95, 52.42) * mm, "end": v(-15.87, 52.41) * mm});
            skLineSegment(sketch, "E793", {"start": v(-16.04, 52.4) * mm, "end": v(-15.95, 52.42) * mm});
            skLineSegment(sketch, "E794", {"start": v(-16.12, 52.39) * mm, "end": v(-16.04, 52.4) * mm});
            skLineSegment(sketch, "E795", {"start": v(-16.2, 52.36) * mm, "end": v(-16.12, 52.39) * mm});
            skLineSegment(sketch, "E796", {"start": v(-16.25, 52.32) * mm, "end": v(-16.2, 52.36) * mm});
            skLineSegment(sketch, "E797", {"start": v(-16.38, 52.2) * mm, "end": v(-16.25, 52.32) * mm});
            skLineSegment(sketch, "E798", {"start": v(-16.6, 51.87) * mm, "end": v(-16.38, 52.2) * mm});
            skLineSegment(sketch, "E799", {"start": v(-17.33, 50.22) * mm, "end": v(-16.6, 51.87) * mm});
            skLineSegment(sketch, "E800", {"start": v(-18.69, 45.97) * mm, "end": v(-17.33, 50.22) * mm});
            skLineSegment(sketch, "E801", {"start": v(-20.28, 41.77) * mm, "end": v(-18.69, 45.97) * mm});
            skLineSegment(sketch, "E802", {"start": v(-21.1, 39.87) * mm, "end": v(-20.28, 41.77) * mm});
            skLineSegment(sketch, "E803", {"start": v(-22.07, 38.03) * mm, "end": v(-21.1, 39.87) * mm});
            skLineSegment(sketch, "E804", {"start": v(-23.27, 36.3) * mm, "end": v(-22.07, 38.03) * mm});
            skLineSegment(sketch, "E805", {"start": v(-24.1, 35.62) * mm, "end": v(-23.27, 36.3) * mm});
            skLineSegment(sketch, "E806", {"start": v(-24.34, 35.45) * mm, "end": v(-24.1, 35.62) * mm});
            skLineSegment(sketch, "E807", {"start": v(-24.63, 35.34) * mm, "end": v(-24.34, 35.45) * mm});
            skLineSegment(sketch, "E808", {"start": v(24.3, 33.07) * mm, "end": v(24.95, 32.84) * mm});
            skLineSegment(sketch, "E809", {"start": v(23.27, 33.28) * mm, "end": v(24.3, 33.07) * mm});
            skLineSegment(sketch, "E810", {"start": v(21.16, 33.56) * mm, "end": v(23.27, 33.28) * mm});
            skLineSegment(sketch, "E811", {"start": v(19.05, 33.84) * mm, "end": v(21.16, 33.56) * mm});
            skLineSegment(sketch, "E812", {"start": v(18.02, 33.83) * mm, "end": v(19.05, 33.84) * mm});
            skLineSegment(sketch, "E813", {"start": v(17.07, 33.62) * mm, "end": v(18.02, 33.83) * mm});
            skLineSegment(sketch, "E814", {"start": v(14.63, 31.56) * mm, "end": v(17.07, 33.62) * mm});
            skLineSegment(sketch, "E815", {"start": v(11.86, 29.8) * mm, "end": v(14.63, 31.56) * mm});
            skLineSegment(sketch, "E816", {"start": v(8.87, 28.47) * mm, "end": v(11.86, 29.8) * mm});
            skLineSegment(sketch, "E817", {"start": v(5.73, 27.57) * mm, "end": v(8.87, 28.47) * mm});
            skLineSegment(sketch, "E818", {"start": v(2.48, 27.11) * mm, "end": v(5.73, 27.57) * mm});
            skLineSegment(sketch, "E819", {"start": v(-0.8, 27.12) * mm, "end": v(2.48, 27.11) * mm});
            skLineSegment(sketch, "E820", {"start": v(-4.03, 27.58) * mm, "end": v(-0.8, 27.12) * mm});
            skLineSegment(sketch, "E821", {"start": v(-7.18, 28.5) * mm, "end": v(-4.03, 27.58) * mm});
            skLineSegment(sketch, "E822", {"start": v(-10.16, 29.85) * mm, "end": v(-7.18, 28.5) * mm});
            skLineSegment(sketch, "E823", {"start": v(-12.93, 31.6) * mm, "end": v(-10.16, 29.85) * mm});
            skLineSegment(sketch, "E824", {"start": v(-15.36, 33.68) * mm, "end": v(-12.93, 31.6) * mm});
            skLineSegment(sketch, "E825", {"start": v(-16.29, 33.92) * mm, "end": v(-15.36, 33.68) * mm});
            skLineSegment(sketch, "E826", {"start": v(-17.26, 33.97) * mm, "end": v(-16.29, 33.92) * mm});
            skLineSegment(sketch, "E827", {"start": v(-19.29, 33.66) * mm, "end": v(-17.26, 33.97) * mm});
            skLineSegment(sketch, "E828", {"start": v(-21.25, 33.12) * mm, "end": v(-19.29, 33.66) * mm});
            skLineSegment(sketch, "E829", {"start": v(-22.13, 32.68) * mm, "end": v(-21.25, 33.12) * mm});
            skLineSegment(sketch, "E830", {"start": v(-22.74, 32.26) * mm, "end": v(-22.13, 32.68) * mm});
            skLineSegment(sketch, "E831", {"start": v(-20.5, 29.62) * mm, "end": v(-22.74, 32.26) * mm});
            skLineSegment(sketch, "E832", {"start": v(-17.74, 27.1) * mm, "end": v(-20.5, 29.62) * mm});
            skLineSegment(sketch, "E833", {"start": v(-14.69, 24.96) * mm, "end": v(-17.74, 27.1) * mm});
            skLineSegment(sketch, "E834", {"start": v(-11.4, 23.2) * mm, "end": v(-14.69, 24.96) * mm});
            skLineSegment(sketch, "E835", {"start": v(-7.9, 21.89) * mm, "end": v(-11.4, 23.2) * mm});
            skLineSegment(sketch, "E836", {"start": v(-4.28, 21) * mm, "end": v(-7.9, 21.89) * mm});
            skLineSegment(sketch, "E837", {"start": v(-0.58, 20.6) * mm, "end": v(-4.28, 21) * mm});
            skLineSegment(sketch, "E838", {"start": v(3.15, 20.64) * mm, "end": v(-0.58, 20.6) * mm});
            skLineSegment(sketch, "E839", {"start": v(6.85, 21.16) * mm, "end": v(3.15, 20.64) * mm});
            skLineSegment(sketch, "E840", {"start": v(10.45, 22.13) * mm, "end": v(6.85, 21.16) * mm});
            skLineSegment(sketch, "E841", {"start": v(13.9, 23.55) * mm, "end": v(10.45, 22.13) * mm});
            skLineSegment(sketch, "E842", {"start": v(17.14, 25.39) * mm, "end": v(13.9, 23.55) * mm});
            skLineSegment(sketch, "E843", {"start": v(20.13, 27.62) * mm, "end": v(17.14, 25.39) * mm});
            skLineSegment(sketch, "E844", {"start": v(22.82, 30.2) * mm, "end": v(20.13, 27.62) * mm});
            skLineSegment(sketch, "E845", {"start": v(24.95, 32.84) * mm, "end": v(22.82, 30.2) * mm});
            skSolve(sketch);
        }
        {
            var Q0;
            Q0=makeQuery(id+"F5.imprint","IMPRINT",FACE,{"disambiguationData":[TD([[makeQuery(id+"F5.imprint","IMPRINT",EDGE,{"derivedFrom":sQuery(id+"F5.wireOp",EDGE,"E424")}),-1.0]])]});
            var Q1;
            Q1=makeQuery(id+"F5.imprint","IMPRINT",FACE,{"disambiguationData":[TD([[makeQuery(id+"F5.imprint","IMPRINT",EDGE,{"derivedFrom":sQuery(id+"F5.wireOp",EDGE,"E511")}),-1.0]])]});
            var Q2;
            Q2=makeQuery(id+"F5.imprint","IMPRINT",FACE,{"disambiguationData":[TD([[makeQuery(id+"F5.imprint","IMPRINT",EDGE,{"derivedFrom":sQuery(id+"F5.wireOp",EDGE,"E628")}),-1.0]])]});
            var Q3;
            Q3=makeQuery(id+"F5.imprint","IMPRINT",FACE,{"disambiguationData":[TD([[makeQuery(id+"F5.imprint","IMPRINT",EDGE,{"derivedFrom":sQuery(id+"F5.wireOp",EDGE,"E808")}),-1.0]])]});
            var Q4;
            Q4=makeQuery(id+"F5.imprint","IMPRINT",FACE,{"disambiguationData":[TD([[makeQuery(id+"F5.imprint","IMPRINT",EDGE,{"derivedFrom":sQuery(id+"F5.wireOp",EDGE,"E750")}),-1.0]])]});
            extrude(context, id + "F6", {"entities" : qUnion([Q0, Q1, Q2, Q3, Q4]), "operationType" : NewBodyOperationType.REMOVE, "oppositeDirection" : true, "depth" : 1.5 * mm});
        }
        {
            var Q0;
            Q0=makeQuery(id+"F1.opExtrude","SWEPT_FACE",FACE,{"disambiguationData":[OSD([sQuery(id+"F0.wireOp",EDGE,"E1.2")])]});
            var sketch = newSketch(context, id + "F7", { "sketchPlane" : qUnion([Q0])});
            skLineSegment(sketch, "E846", {"start": v(-38, 96) * mm, "end": v(38, 96) * mm, "construction": true});
            skLineSegment(sketch, "E847", {"start": v(35, 101) * mm, "end": v(35, 0) * mm, "construction": true});
            skLineSegment(sketch, "E848", {"start": v(35, 0) * mm, "end": v(34.25, 0.51) * mm, "construction": true});
            skLineSegment(sketch, "E849", {"start": v(-35, 101) * mm, "end": v(-35, 0) * mm, "construction": true});
            skLineSegment(sketch, "E850", {"start": v(-35, 0) * mm, "end": v(-35.75, 0.27) * mm, "construction": true});
            skLineSegment(sketch, "E851", {"start": v(-35, 101) * mm, "end": v(-36.5, 96) * mm});
            skLineSegment(sketch, "E852", {"start": v(-36.5, 96) * mm, "end": v(36.5, 96) * mm});
            skLineSegment(sketch, "E853", {"start": v(36.5, 96) * mm, "end": v(35, 101) * mm});
            skSolve(sketch);
        }
        {
            var Q0;
            {var subQ0=sQuery(id+"F7.wireOp",EDGE,"E851");Q0=makeQuery(id+"F7.imprint","IMPRINT",FACE,{"disambiguationData":[TD([[makeQuery(id+"F7.imprint","IMPRINT",EDGE,{"derivedFrom":subQ0}),1.0]])]});}
            var Q1;
            Q1=makeQuery(id+"F2.opShell","OFFSET_FACE",FACE,{"disambiguationData":[OSD([sQuery(id+"F0.wireOp",EDGE,"E1.0")])]});
            extrude(context, id + "F8", {"entities" : qUnion([Q0]), "operationType" : NewBodyOperationType.REMOVE, "endBound" : BoundingType.UP_TO_SURFACE, "oppositeDirection" : true, "endBoundEntityFace" : qUnion([Q1]), "depth" : 25 * mm});
        }
        {
            var Q0;
            Q0=makeQuery(id+"F1.opExtrude","SWEPT_FACE",FACE,{"disambiguationData":[OSD([sQuery(id+"F0.wireOp",EDGE,"E1.2")])]});
            var sketch = newSketch(context, id + "F9", { "sketchPlane" : qUnion([Q0])});
            skLineSegment(sketch, "E854.0", {"start": v(-35, 101) * mm, "end": v(-36.5, 96) * mm});
            skLineSegment(sketch, "E854.1", {"start": v(-36.5, 96) * mm, "end": v(36.5, 96) * mm});
            skLineSegment(sketch, "E854.2", {"start": v(36.5, 96) * mm, "end": v(35, 101) * mm});
            skLineSegment(sketch, "E854.3", {"start": v(35, 101) * mm, "end": v(-35, 101) * mm});
            skLineSegment(sketch, "E855", {"start": v(34.48, 101) * mm, "end": v(35.98, 96) * mm});
            skSolve(sketch);
        }
        {
            var Q0;
            {var subQ0=sQuery(id+"F9.wireOp",EDGE,"E854.0");Q0=makeQuery(id+"F9.imprint","IMPRINT",FACE,{"disambiguationData":[TD([[makeQuery(id+"F9.imprint","IMPRINT",EDGE,{"derivedFrom":subQ0}),1.0]])]});}
            var Q1;
            Q1=makeQuery(id+"F8.boolean.opBoolean","MERGE",FACE,{"derivedFrom":[makeQuery(id+"F2.opShell","OFFSET_FACE",FACE,{"disambiguationData":[OSD([sQuery(id+"F0.wireOp",EDGE,"E1.0")])]}),makeQuery(id+"F8.opExtrude","CAP_FACE",FACE,{"disambiguationData":[OSD([sQuery(id+"F0.wireOp",EDGE,"E1.2"),sQuery(id+"F7.wireOp",EDGE,"E851"),sQuery(id+"F7.wireOp",EDGE,"E852"),sQuery(id+"F7.wireOp",EDGE,"E853")])],"isStart":false})]});
            extrude(context, id + "F10", {"entities" : qUnion([Q0]), "endBound" : BoundingType.UP_TO_SURFACE, "oppositeDirection" : true, "endBoundEntityFace" : qUnion([Q1]), "depth" : 25 * mm});
        }
        {
            var Q0;
            Q0=makeQuery(id+"F10.opExtrude","SWEPT_BODY",BODY,{"disambiguationData":[OSD([sQuery(id+"F9.wireOp",EDGE,"E854.0"),sQuery(id+"F9.wireOp",EDGE,"E854.1"),sQuery(id+"F9.wireOp",EDGE,"E854.3"),sQuery(id+"F9.wireOp",EDGE,"E855")])]});
            var Q1;
            Q1=makeQuery(id+"F1.opExtrude","SWEPT_FACE",FACE,{"disambiguationData":[OSD([sQuery(id+"F0.wireOp",EDGE,"E1.3")])]});
            transform(context, id + "F11", {"entities" : qUnion([Q0]), "transformType" : TransformType.TRANSLATION_DISTANCE, "transformDirection" : qUnion([Q1]), "distance" : 90 * mm, "makeCopy" : true});
        }
        {
            var Q0;
            Q0=makeQuery(id+"F10.opExtrude","SWEPT_FACE",FACE,{"disambiguationData":[OSD([sQuery(id+"F9.wireOp",EDGE,"E854.3")])]});
            var sketch = newSketch(context, id + "F12", { "sketchPlane" : qUnion([Q0])});
            skLineSegment(sketch, "E856", {"start": v(-0.26, -38) * mm, "end": v(-0.26, 35) * mm, "construction": true});
            skLineSegment(sketch, "E857", {"start": v(-35, -33) * mm, "end": v(34.48, -33) * mm, "construction": true});
            skArc(sketch, "E858", {"start": v(12.24, -33) * mm, "mid": v(-0.26, -20.5) * mm, "end": v(-12.76, -33) * mm});
            skLineSegment(sketch, "E859", {"start": v(-12.76, -33) * mm, "end": v(12.24, -33) * mm});
            skSolve(sketch);
        }
        {
            var Q0;
            Q0=makeQuery(id+"F12.imprint","IMPRINT",FACE,{"disambiguationData":[TD([[makeQuery(id+"F12.imprint","IMPRINT",EDGE,{"derivedFrom":sQuery(id+"F12.wireOp",EDGE,"E858")}),1.0]])]});
            extrude(context, id + "F13", {"entities" : qUnion([Q0]), "operationType" : NewBodyOperationType.REMOVE, "oppositeDirection" : true, "depth" : 2 * mm});
        }
        {
            var Q0;
            Q0=makeQuery(id+"F13.boolean.opBoolean","COPY",EDGE,{"derivedFrom":makeQuery(id+"F13.opExtrude","CAP_EDGE",EDGE,{"disambiguationData":[OSD([sQuery(id+"F12.wireOp",EDGE,"E858")])],"isStart":false})});
            fillet(context, id + "F14", {"entities" : qUnion([Q0]), "radius" : 5 * mm, "tangentPropagation" : true, "allowEdgeOverflow" : false});
        }
        {
            var Q0;
            Q0=makeQuery(id+"F10.opExtrude","CAP_FACE",FACE,{"disambiguationData":[OSD([sQuery(id+"F9.wireOp",EDGE,"E854.0"),sQuery(id+"F9.wireOp",EDGE,"E854.1"),sQuery(id+"F9.wireOp",EDGE,"E854.3"),sQuery(id+"F9.wireOp",EDGE,"E855")])],"isStart":true});
            extrude(context, id + "F15", {"entities" : qUnion([Q0]), "operationType" : NewBodyOperationType.REMOVE, "oppositeDirection" : true, "depth" : 0.2 * mm});
        }
        {
            var Q0;
            Q0=makeQuery(id+"F10.opExtrude","SWEPT_BODY",BODY,{"disambiguationData":[OSD([sQuery(id+"F9.wireOp",EDGE,"E854.0"),sQuery(id+"F9.wireOp",EDGE,"E854.1"),sQuery(id+"F9.wireOp",EDGE,"E854.3"),sQuery(id+"F9.wireOp",EDGE,"E855")])]});
            var Q1;
            Q1=makeQuery(id+"F1.opExtrude","SWEPT_FACE",FACE,{"disambiguationData":[OSD([sQuery(id+"F0.wireOp",EDGE,"E1.1")])]});
            transform(context, id + "F16", {"entities" : qUnion([Q0]), "transformType" : TransformType.TRANSLATION_DISTANCE, "transformDirection" : qUnion([Q1]), "distance" : 80 * mm, "makeCopy" : true});
        }
        {
            var Q0;
            Q0=makeQuery(id+"F16.opPattern","COPY",FACE,{"derivedFrom":makeQuery(id+"F10.opExtrude","SWEPT_FACE",FACE,{"disambiguationData":[OSD([sQuery(id+"F9.wireOp",EDGE,"E854.3")])]}),"instanceName":"1"});
            var sketch = newSketch(context, id + "F17", { "sketchPlane" : qUnion([Q0])});
            skLineSegment(sketch, "E860", {"start": v(79.74, 35) * mm, "end": v(79.74, -37.8) * mm, "construction": true});
            skText(sketch, "E861", { "text": "Charles", "fontName": "OpenSans-Bold.ttf"});
            skText(sketch, "E862", { "text": "Drake", "fontName": "OpenSans-Bold.ttf"});
            const initialGuessF17  = {"E861": [0.04884, 0.006, 1, 0, 0.012], "E862": [0.05502, -0.011, 1, 0, 0.012]};
            skSetInitialGuess(sketch, initialGuessF17);
            skSolve(sketch);
        }
        {
            var Q0;
            Q0 = qSketchRegion(id + "F17", true);
            extrude(context, id + "F18", {"entities" : qUnion([Q0]), "operationType" : NewBodyOperationType.REMOVE, "oppositeDirection" : true, "depth" : 1.7 * mm});
        }
        {
            var Q0;
            Q0=makeQuery(id+"F10.opExtrude","SWEPT_BODY",BODY,{"disambiguationData":[OSD([sQuery(id+"F9.wireOp",EDGE,"E854.0"),sQuery(id+"F9.wireOp",EDGE,"E854.1"),sQuery(id+"F9.wireOp",EDGE,"E854.3"),sQuery(id+"F9.wireOp",EDGE,"E855")])]});
            var Q1;
            Q1=makeQuery(id+"F1.opExtrude","SWEPT_FACE",FACE,{"disambiguationData":[OSD([sQuery(id+"F0.wireOp",EDGE,"E1.1")])]});
            transform(context, id + "F19", {"entities" : qUnion([Q0]), "transformType" : TransformType.TRANSLATION_DISTANCE, "transformDirection" : qUnion([Q1]), "distance" : 160 * mm, "makeCopy" : true});
        }
        {
            var Q0;
            Q0=makeQuery(id+"F19.opPattern","COPY",FACE,{"derivedFrom":makeQuery(id+"F10.opExtrude","SWEPT_FACE",FACE,{"disambiguationData":[OSD([sQuery(id+"F9.wireOp",EDGE,"E854.3")])]}),"instanceName":"1"});
            var sketch = newSketch(context, id + "F20", { "sketchPlane" : qUnion([Q0])});
            skText(sketch, "E863", { "text": "Nathan", "fontName": "OpenSans-Bold.ttf"});
            skLineSegment(sketch, "E864", {"start": v(159.74, 35) * mm, "end": v(159.74, -37.8) * mm, "construction": true});
            skText(sketch, "E865", { "text": "Drake", "fontName": "OpenSans-Bold.ttf"});
            const initialGuessF20  = {"E863": [0.12841, 0.007, 1, 0, 0.012], "E865": [0.13448, -0.01, 1, 0, 0.012]};
            skSetInitialGuess(sketch, initialGuessF20);
            skSolve(sketch);
        }
        {
            var Q0;
            Q0 = qSketchRegion(id + "F20", true);
            extrude(context, id + "F21", {"entities" : qUnion([Q0]), "operationType" : NewBodyOperationType.REMOVE, "oppositeDirection" : true, "depth" : 1.7 * mm});
        }
        {
            var Q0;
            Q0=makeQuery(id+"F10.opExtrude","SWEPT_BODY",BODY,{"disambiguationData":[OSD([sQuery(id+"F9.wireOp",EDGE,"E854.0"),sQuery(id+"F9.wireOp",EDGE,"E854.1"),sQuery(id+"F9.wireOp",EDGE,"E854.3"),sQuery(id+"F9.wireOp",EDGE,"E855")])]});
            var Q1;
            Q1=makeQuery(id+"F1.opExtrude","SWEPT_FACE",FACE,{"disambiguationData":[OSD([sQuery(id+"F0.wireOp",EDGE,"E1.1")])]});
            transform(context, id + "F22", {"entities" : qUnion([Q0]), "transformType" : TransformType.TRANSLATION_DISTANCE, "transformDirection" : qUnion([Q1]), "distance" : 240 * mm, "makeCopy" : true});
        }
        {
            var Q0;
            Q0=makeQuery(id+"F22.opPattern","COPY",FACE,{"derivedFrom":makeQuery(id+"F10.opExtrude","SWEPT_FACE",FACE,{"disambiguationData":[OSD([sQuery(id+"F9.wireOp",EDGE,"E854.3")])]}),"instanceName":"1"});
            var sketch = newSketch(context, id + "F23", { "sketchPlane" : qUnion([Q0])});
            skText(sketch, "E866", { "text": "Danielle", "fontName": "OpenSans-Bold.ttf"});
            skText(sketch, "E867", { "text": "Bishop", "fontName": "OpenSans-Bold.ttf"});
            skLineSegment(sketch, "E868", {"start": v(239.74, 35) * mm, "end": v(239.74, -37.8) * mm, "construction": true});
            const initialGuessF23  = {"E866": [0.2054, 0.007, 1, 0, 0.012], "E867": [0.21138, -0.01, 1, 0, 0.012]};
            skSetInitialGuess(sketch, initialGuessF23);
            skSolve(sketch);
        }
        {
            var Q0;
            Q0 = qSketchRegion(id + "F23", true);
            extrude(context, id + "F24", {"entities" : qUnion([Q0]), "operationType" : NewBodyOperationType.REMOVE, "oppositeDirection" : true, "depth" : 1.7 * mm, "offsetDistance" : 25 * mm});
        }
    });
